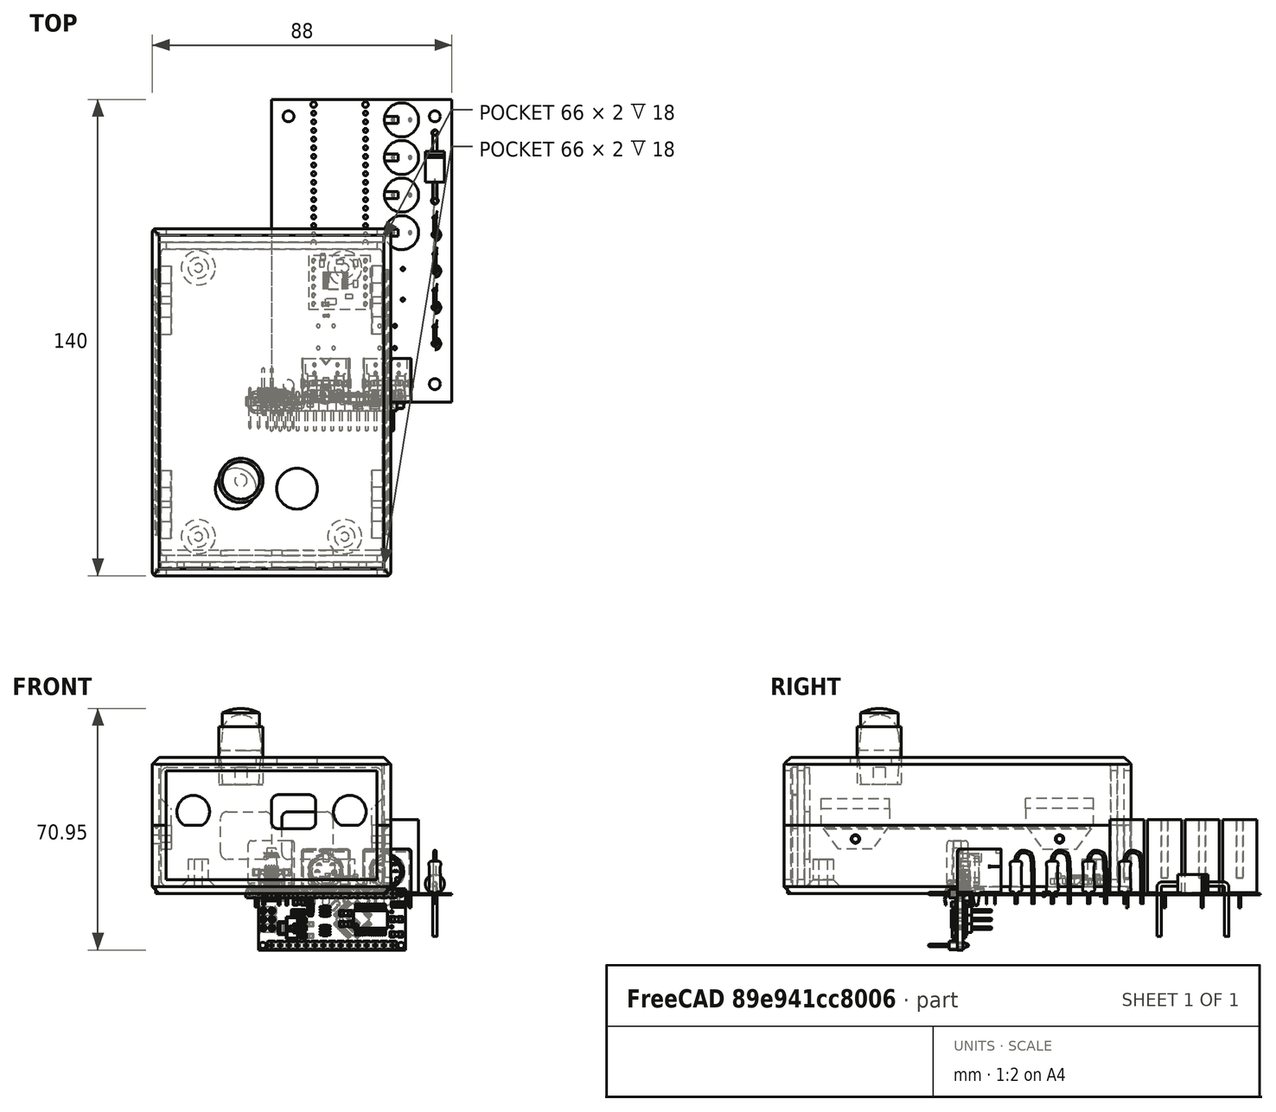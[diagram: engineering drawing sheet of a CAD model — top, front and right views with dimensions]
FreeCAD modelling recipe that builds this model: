
FCSTD DOCUMENT  (FreeCAD 1.0R39109 (Git))
Label: box
License: All rights reserved
LicenseURL: https://en.wikipedia.org/wiki/All_rights_reserved
objects: Part::Feature×156, App::Part×50, Sketcher::SketchObject×21, PartDesign::Pocket×11, PartDesign::Pad×7, PartDesign::Mirrored×7, App::Link×7, App::FeaturePython×7, PartDesign::Fillet×6, PartDesign::Body×6, PartDesign::Chamfer×5, PartDesign::Plane×2, PartDesign::Revolution×2, Mesh::Feature×1, PartDesign::MultiTransform×1, Assembly::JointGroup×1, Assembly::AssemblyObject×1
note: 315 computed .brp shape members not serialized (recipe doc carries the construction recipe); baked Part::Feature solids carry a one-line shape summary decoded from their .brp

FEATURE [Part::Feature] Part__Feature  label="Open CASCADE STEP translator 7.5 1.1.1"
  Placement = pos=(0,0,-0.41148) rot=(0,0,1;0rad)
  shape: bbox 53 x 89 x 0.4115 mm, 116 faces (baked)
FEATURE [App::Part] Board
  Group = -> [Part__Feature]
  Origin = -> Origin
FEATURE [Part::Feature] Part__Feature001  label="R603"
  Placement = pos=(34.1248,25.4,0) rot=(0,0.707107,0.707107;3.14159rad)
  shape: bbox 1.6 x 0.8 x 0.302 mm, 90 faces (baked)
FEATURE [App::Part] R4
  Group = -> [Part__Feature001]
  Origin = -> Origin001
FEATURE [Part::Feature] Part__Feature002  label="C0603"
  Placement = pos=(33.2994,25.7937,-0.41148) rot=(-1,0,0;1.5708rad)
  shape: bbox 1.6 x 0.8 x 0.5 mm, 44 faces (baked)
FEATURE [App::Part] C2
  Group = -> [Part__Feature002]
  Origin = -> Origin002
FEATURE [Part::Feature] Part__Feature003  label="R604"
  Placement = pos=(16.0749,25.3999,0) rot=(0,0.707107,0.707107;3.14159rad)
  shape: bbox 1.6 x 0.8 x 0.302 mm, 90 faces (baked)
FEATURE [App::Part] R3
  Group = -> [Part__Feature003]
  Origin = -> Origin003
FEATURE [Part::Feature] Part__Feature004  label="C0604"
  Placement = pos=(15.2994,25.7937,-0.41148) rot=(-1,0,0;1.5708rad)
  shape: bbox 1.6 x 0.8 x 0.5 mm, 44 faces (baked)
FEATURE [App::Part] C1
  Group = -> [Part__Feature004]
  Origin = -> Origin004
FEATURE [Part::Feature] Part__Feature005  label="1"
  shape: bbox 0.6 x 0.6 x 4.5 mm, 4 faces (baked)
FEATURE [Part::Feature] Part__Feature006  label="1001"
  shape: bbox 0.6 x 0.6 x 4 mm, 4 faces (baked)
FEATURE [App::Part] _  label="1002"
  Group = -> [Part__Feature005,Part__Feature006]
  Origin = -> Origin005
FEATURE [Part::Feature] Part__Feature007  label="2"
  shape: bbox 11.96 x 4.66 x 0.5 mm, 10 faces (baked)
FEATURE [Part::Feature] Part__Feature008  label="3"
  shape: bbox 0.8199 x 2.3 x 15.48 mm, 17 faces (baked)
FEATURE [Part::Feature] Part__Feature009  label="4"
  shape: bbox 13.93 x 6.63 x 15.5 mm, 101 faces (baked)
FEATURE [Part::Feature] Part__Feature010  label="AVX Logo 2"
  Placement = pos=(2.33024,3.051,15.4348) rot=(0,0.707107,0.707107;3.14159rad)
  shape: bbox 0.9574 x 0.1 x 1.177 mm, 8 faces (baked)
FEATURE [Part::Feature] Part__Feature011  label="AVX Logo 003"
  Placement = pos=(2.33024,3.051,15.4348) rot=(0,0.707107,0.707107;3.14159rad)
  shape: bbox 0.6063 x 0.1 x 1.597 mm, 8 faces (baked)
FEATURE [Part::Feature] Part__Feature012  label="AVX Logo 004"
  Placement = pos=(2.33024,3.051,15.4348) rot=(0,0.707107,0.707107;3.14159rad)
  shape: bbox 0.9677 x 0.1 x 0.5254 mm, 10 faces (baked)
FEATURE [Part::Feature] Part__Feature013  label="AVX Logo 005"
  Placement = pos=(2.33024,3.051,15.4348) rot=(0,0.707107,0.707107;3.14159rad)
  shape: bbox 0.3209 x 0.1 x 0.3907 mm, 5 faces (baked)
FEATURE [Part::Feature] Part__Feature014  label="AVX Logo 006"
  Placement = pos=(2.33024,3.051,15.4348) rot=(0,0.707107,0.707107;3.14159rad)
  shape: bbox 0.2898 x 0.1 x 0.3547 mm, 5 faces (baked)
FEATURE [Part::Feature] Part__Feature015  label="AVX Logo 007"
  Placement = pos=(2.33024,3.051,15.4348) rot=(0,0.707107,0.707107;3.14159rad)
  shape: bbox 0.3208 x 0.1 x 0.3911 mm, 5 faces (baked)
FEATURE [Part::Feature] Part__Feature016  label="AVX Logo 008"
  Placement = pos=(2.33024,3.051,15.4348) rot=(0,0.707107,0.707107;3.14159rad)
  shape: bbox 0.9255 x 0.1 x 1.591 mm, 6 faces (baked)
FEATURE [Part::Feature] Part__Feature017  label="AVX Logo 009"
  Placement = pos=(2.33024,3.051,15.4348) rot=(0,0.707107,0.707107;3.14159rad)
  shape: bbox 0.9743 x 0.1 x 1.58 mm, 6 faces (baked)
FEATURE [Part::Feature] Part__Feature018  label="AVX Logo 010"
  Placement = pos=(2.33024,3.051,15.4348) rot=(0,0.707107,0.707107;3.14159rad)
  shape: bbox 1.209 x 0.1 x 1.602 mm, 11 faces (baked)
FEATURE [App::Part] AVX_Logo_2  label="AVX Logo 011"
  Group = -> [Part__Feature010,Part__Feature011,Part__Feature012,Part__Feature013,Part__Feature014,Part__Feature015,Part__Feature016,Part__Feature017,Part__Feature018]
  Origin = -> Origin006
FEATURE [App::Part] Cap_AVX_SCMQ14C474PRBA0_eec
  Group = -> [_,Part__Feature007,Part__Feature008,Part__Feature009,AVX_Logo_2]
  Origin = -> Origin007
  Placement = pos=(38.608,34.6712,0) rot=(0,0,-1;1.5708rad)
FEATURE [App::Part] C7
  Group = -> [Cap_AVX_SCMQ14C474PRBA0_eec]
  Origin = -> Origin008
FEATURE [Part::Feature] Part__Feature019  label="DO-201AD"
  Placement = pos=(48,69.1712,0) rot=(0.57735,-0.57735,-0.57735;2.0944rad)
  shape: bbox 5.6 x 0.8 x 5.6 mm, 6 faces (baked)
FEATURE [Part::Feature] Part__Feature020  label="DO-201AD001"
  Placement = pos=(48,69.1712,0) rot=(0.57735,-0.57735,-0.57735;2.0944rad)
  shape: bbox 5.6 x 9 x 5.6 mm, 10 faces (baked)
FEATURE [Part::Feature] Part__Feature021  label="DO-201AD002"
  Placement = pos=(48,69.1712,0) rot=(0.57735,-0.57735,-0.57735;2.0944rad)
  shape: bbox 1.25 x 6.209 x 16.21 mm, 8 faces (baked)
FEATURE [Part::Feature] Part__Feature022  label="DO-201AD003"
  Placement = pos=(48,69.1712,0) rot=(0.57735,-0.57735,-0.57735;2.0944rad)
  shape: bbox 1.25 x 6.209 x 16.21 mm, 8 faces (baked)
FEATURE [App::Part] DO_201AD  label="DO-201AD004"
  Group = -> [Part__Feature019,Part__Feature020,Part__Feature021,Part__Feature022]
  Origin = -> Origin009
FEATURE [App::Part] D3
  Group = -> [DO_201AD]
  Origin = -> Origin010
FEATURE [Part::Feature] Part__Feature023  label="RESISTOR_2W_VERTICALE"
  Placement = pos=(48.0001,27.8623,22) rot=(0.57735,-0.57735,-0.57735;2.0944rad)
  shape: bbox 7.092 x 7.627 x 16.21 mm, 28 faces (baked)
FEATURE [App::Part] R8
  Group = -> [Part__Feature023]
  Origin = -> Origin011
FEATURE [Part::Feature] Part__Feature024  label="RESISTOR_2W_VERTICALE001"
  Placement = pos=(48.0001,17.1892,22) rot=(0.57735,-0.57735,-0.57735;2.0944rad)
  shape: bbox 7.092 x 7.627 x 16.21 mm, 28 faces (baked)
FEATURE [App::Part] R7
  Group = -> [Part__Feature024]
  Origin = -> Origin012
FEATURE [Part::Feature] Part__Feature025  label="RESISTOR_2W_VERTICALE002"
  Placement = pos=(48.0001,49.2084,22) rot=(0.57735,-0.57735,-0.57735;2.0944rad)
  shape: bbox 7.092 x 7.627 x 16.21 mm, 28 faces (baked)
FEATURE [App::Part] R6
  Group = -> [Part__Feature025]
  Origin = -> Origin013
FEATURE [Part::Feature] Part__Feature026  label="RESISTOR_2W_VERTICALE003"
  Placement = pos=(48.0001,38.5353,22) rot=(0.57735,-0.57735,-0.57735;2.0944rad)
  shape: bbox 7.092 x 7.627 x 16.21 mm, 28 faces (baked)
FEATURE [App::Part] R5
  Group = -> [Part__Feature026]
  Origin = -> Origin014
FEATURE [Part::Feature] Part__Feature027  label="CAP_RN_10X20_NCH"
  Placement = pos=(40.727,60.873,0.2) rot=(0,0,1;3.14159rad)
  shape: bbox 0.6096 x 0.6096 x 4.369 mm, 3 faces (baked)
FEATURE [Part::Feature] Part__Feature028  label="CAP_RN_10X20_NCH001"
  Placement = pos=(40.727,60.873,0.2) rot=(0,0,1;3.14159rad)
  shape: bbox 0.6096 x 0.6096 x 4.369 mm, 3 faces (baked)
FEATURE [Part::Feature] Part__Feature029  label="CAP_RN_10X20_NCH002"
  Placement = pos=(40.727,60.873,0.2) rot=(0,0,1;3.14159rad)
  shape: bbox 10.01 x 10.01 x 21.49 mm, 3 faces (baked)
FEATURE [Part::Feature] Part__Feature030  label="CAP_RN_10X20_NCH003"
  Placement = pos=(40.727,60.873,0.2) rot=(0,0,1;3.14159rad)
  shape: bbox 4.029 x 1.953 x 17.22 mm, 8 faces (baked)
FEATURE [App::Part] CAP_RN_10X20_NCH  label="CAP_RN_10X20_NCH004"
  Group = -> [Part__Feature027,Part__Feature028,Part__Feature029,Part__Feature030]
  Origin = -> Origin015
FEATURE [App::Part] C5
  Group = -> [CAP_RN_10X20_NCH]
  Origin = -> Origin016
FEATURE [Part::Feature] Part__Feature031  label="CAP_RN_10X20_NCH005"
  Placement = pos=(40.727,71.922,0.2) rot=(0,0,1;3.14159rad)
  shape: bbox 0.6096 x 0.6096 x 4.369 mm, 3 faces (baked)
FEATURE [Part::Feature] Part__Feature032  label="CAP_RN_10X20_NCH006"
  Placement = pos=(40.727,71.922,0.2) rot=(0,0,1;3.14159rad)
  shape: bbox 0.6096 x 0.6096 x 4.369 mm, 3 faces (baked)
FEATURE [Part::Feature] Part__Feature033  label="CAP_RN_10X20_NCH007"
  Placement = pos=(40.727,71.922,0.2) rot=(0,0,1;3.14159rad)
  shape: bbox 10.01 x 10.01 x 21.49 mm, 3 faces (baked)
FEATURE [Part::Feature] Part__Feature034  label="CAP_RN_10X20_NCH008"
  Placement = pos=(40.727,71.922,0.2) rot=(0,0,1;3.14159rad)
  shape: bbox 4.029 x 1.953 x 17.22 mm, 8 faces (baked)
FEATURE [App::Part] CAP_RN_10X20_NCH001  label="CAP_RN_10X20_NCH009"
  Group = -> [Part__Feature031,Part__Feature032,Part__Feature033,Part__Feature034]
  Origin = -> Origin017
FEATURE [App::Part] C4
  Group = -> [CAP_RN_10X20_NCH001]
  Origin = -> Origin018
FEATURE [Part::Feature] Part__Feature035  label="CAP_RN_10X20_NCH010"
  Placement = pos=(40.727,82.971,0.2) rot=(0,0,1;3.14159rad)
  shape: bbox 0.6096 x 0.6096 x 4.369 mm, 3 faces (baked)
FEATURE [Part::Feature] Part__Feature036  label="CAP_RN_10X20_NCH011"
  Placement = pos=(40.727,82.971,0.2) rot=(0,0,1;3.14159rad)
  shape: bbox 0.6096 x 0.6096 x 4.369 mm, 3 faces (baked)
FEATURE [Part::Feature] Part__Feature037  label="CAP_RN_10X20_NCH012"
  Placement = pos=(40.727,82.971,0.2) rot=(0,0,1;3.14159rad)
  shape: bbox 10.01 x 10.01 x 21.49 mm, 3 faces (baked)
FEATURE [Part::Feature] Part__Feature038  label="CAP_RN_10X20_NCH013"
  Placement = pos=(40.727,82.971,0.2) rot=(0,0,1;3.14159rad)
  shape: bbox 4.029 x 1.953 x 17.22 mm, 8 faces (baked)
FEATURE [App::Part] CAP_RN_10X20_NCH002  label="CAP_RN_10X20_NCH014"
  Group = -> [Part__Feature035,Part__Feature036,Part__Feature037,Part__Feature038]
  Origin = -> Origin019
FEATURE [App::Part] C3
  Group = -> [CAP_RN_10X20_NCH002]
  Origin = -> Origin020
FEATURE [Part::Feature] Part__Feature039  label="CAP_RN_10X20_NCH015"
  Placement = pos=(40.727,49.824,0.2) rot=(0,0,1;3.14159rad)
  shape: bbox 0.6096 x 0.6096 x 4.369 mm, 3 faces (baked)
FEATURE [Part::Feature] Part__Feature040  label="CAP_RN_10X20_NCH016"
  Placement = pos=(40.727,49.824,0.2) rot=(0,0,1;3.14159rad)
  shape: bbox 0.6096 x 0.6096 x 4.369 mm, 3 faces (baked)
FEATURE [Part::Feature] Part__Feature041  label="CAP_RN_10X20_NCH017"
  Placement = pos=(40.727,49.824,0.2) rot=(0,0,1;3.14159rad)
  shape: bbox 10.01 x 10.01 x 21.49 mm, 3 faces (baked)
FEATURE [Part::Feature] Part__Feature042  label="CAP_RN_10X20_NCH018"
  Placement = pos=(40.727,49.824,0.2) rot=(0,0,1;3.14159rad)
  shape: bbox 4.029 x 1.953 x 17.22 mm, 8 faces (baked)
FEATURE [App::Part] CAP_RN_10X20_NCH003  label="CAP_RN_10X20_NCH019"
  Group = -> [Part__Feature039,Part__Feature040,Part__Feature041,Part__Feature042]
  Origin = -> Origin021
FEATURE [App::Part] C6
  Group = -> [CAP_RN_10X20_NCH003]
  Origin = -> Origin022
FEATURE [Part::Feature] Part__Feature043  label="arm"
  Placement = pos=(0,0,13) rot=(0,0,1;0rad)
  shape: bbox 3.51 x 3.51 x 9.7 mm, 4 faces (baked)
FEATURE [Part::Feature] Part__Feature044  label="body"
  Placement = pos=(0,0,13) rot=(0,0,1;0rad)
  shape: bbox 5.99 x 5.99 x 3.9 mm, 22 faces (baked)
FEATURE [Part::Feature] Part__Feature045  label="leads"
  Placement = pos=(0,0,13) rot=(0,0,1;0rad)
  shape: bbox 0.71 x 0.905 x 4.81 mm, 16 faces (baked)
FEATURE [Part::Feature] Part__Feature046  label="leads001"
  Placement = pos=(0,0,13) rot=(0,0,1;0rad)
  shape: bbox 0.71 x 0.905 x 4.81 mm, 16 faces (baked)
FEATURE [Part::Feature] Part__Feature047  label="leads002"
  Placement = pos=(0,0,13) rot=(0,0,1;0rad)
  shape: bbox 0.71 x 0.905 x 4.81 mm, 16 faces (baked)
FEATURE [Part::Feature] Part__Feature048  label="leads003"
  Placement = pos=(0,0,13) rot=(0,0,1;0rad)
  shape: bbox 0.71 x 0.905 x 4.81 mm, 16 faces (baked)
FEATURE [App::Part] leads  label="leads004"
  Group = -> [Part__Feature045,Part__Feature046,Part__Feature047,Part__Feature048]
  Origin = -> Origin023
FEATURE [Part::Feature] Part__Feature049  label="top"
  Placement = pos=(0,0,13) rot=(0,0,1;0rad)
  shape: bbox 5.99 x 5.99 x 0.1 mm, 14 faces (baked)
FEATURE [Part::Feature] Part__Feature050  label="TE Connectivity"
  Placement = pos=(-2.995,0.1796,1.65363) rot=(0.57735,-0.57735,-0.57735;2.0944rad)
  shape: bbox 0.003004 x 0.8535 x 0.7964 mm, 15 faces (baked)
FEATURE [Part::Feature] Part__Feature051  label="TE Connectivity001"
  Placement = pos=(-2.995,0.1796,1.65363) rot=(0.57735,-0.57735,-0.57735;2.0944rad)
  shape: bbox 0.003 x 0.7442 x 0.7964 mm, 11 faces (baked)
FEATURE [Part::Feature] Part__Feature052  label="TE Connectivity002"
  Placement = pos=(-2.995,0.1796,1.65363) rot=(0.57735,-0.57735,-0.57735;2.0944rad)
  shape: bbox 0.003601 x 1.019 x 0.2312 mm, 10 faces (baked)
FEATURE [Part::Feature] Part__Feature053  label="TE Connectivity003"
  Placement = pos=(-2.995,0.1796,1.65363) rot=(0.57735,-0.57735,-0.57735;2.0944rad)
  shape: bbox 0.0036 x 1.019 x 0.2312 mm, 8 faces (baked)
FEATURE [Part::Feature] Part__Feature054  label="TE Connectivity004"
  Placement = pos=(-2.995,0.1796,1.65363) rot=(0.57735,-0.57735,-0.57735;2.0944rad)
  shape: bbox 0.0036 x 1.019 x 0.2312 mm, 8 faces (baked)
FEATURE [Part::Feature] Part__Feature055  label="TE Connectivity005"
  Placement = pos=(-2.995,0.1796,1.65363) rot=(0.57735,-0.57735,-0.57735;2.0944rad)
  shape: bbox 0.003645 x 0.1539 x 0.16 mm, 13 faces (baked)
FEATURE [Part::Feature] Part__Feature056  label="TE Connectivity006"
  Placement = pos=(-2.995,0.1796,1.65363) rot=(0.57735,-0.57735,-0.57735;2.0944rad)
  shape: bbox 0.00365 x 0.1344 x 0.1238 mm, 18 faces (baked)
FEATURE [Part::Feature] Part__Feature057  label="TE Connectivity007"
  Placement = pos=(-2.995,0.1796,1.65363) rot=(0.57735,-0.57735,-0.57735;2.0944rad)
  shape: bbox 0.003601 x 0.1303 x 0.1287 mm, 16 faces (baked)
FEATURE [Part::Feature] Part__Feature058  label="TE Connectivity008"
  Placement = pos=(-2.995,0.1796,1.65363) rot=(0.57735,-0.57735,-0.57735;2.0944rad)
  shape: bbox 0.003684 x 0.1335 x 0.1245 mm, 18 faces (baked)
FEATURE [Part::Feature] Part__Feature059  label="TE Connectivity009"
  Placement = pos=(-2.995,0.1796,1.65363) rot=(0.57735,-0.57735,-0.57735;2.0944rad)
  shape: bbox 0.003695 x 0.1252 x 0.1305 mm, 16 faces (baked)
FEATURE [Part::Feature] Part__Feature060  label="TE Connectivity010"
  Placement = pos=(-2.995,0.1796,1.65363) rot=(0.57735,-0.57735,-0.57735;2.0944rad)
  shape: bbox 0.004453 x 0.08777 x 0.1574 mm, 23 faces (baked)
FEATURE [Part::Feature] Part__Feature061  label="TE Connectivity011"
  Placement = pos=(-2.995,0.1796,1.65363) rot=(0.57735,-0.57735,-0.57735;2.0944rad)
  shape: bbox 0.003603 x 0.1223 x 0.1299 mm, 15 faces (baked)
FEATURE [Part::Feature] Part__Feature062  label="TE Connectivity012"
  Placement = pos=(-2.995,0.1796,1.65363) rot=(0.57735,-0.57735,-0.57735;2.0944rad)
  shape: bbox 0.003805 x 0.1229 x 0.1291 mm, 20 faces (baked)
FEATURE [Part::Feature] Part__Feature063  label="TE Connectivity013"
  Placement = pos=(-2.995,0.1796,1.65363) rot=(0.57735,-0.57735,-0.57735;2.0944rad)
  shape: bbox 0.003627 x 0.0856 x 0.1551 mm, 24 faces (baked)
FEATURE [Part::Feature] Part__Feature064  label="TE Connectivity014"
  Placement = pos=(-2.995,0.1796,1.65363) rot=(0.57735,-0.57735,-0.57735;2.0944rad)
  shape: bbox 0.003 x 0.1246 x 0.1226 mm, 9 faces (baked)
FEATURE [Part::Feature] Part__Feature065  label="TE Connectivity015"
  Placement = pos=(-2.995,0.1796,1.65363) rot=(0.57735,-0.57735,-0.57735;2.0944rad)
  shape: bbox 0.003 x 0.0679 x 0.1237 mm, 6 faces (baked)
FEATURE [Part::Feature] Part__Feature066  label="TE Connectivity016"
  Placement = pos=(-2.995,0.1796,1.65363) rot=(0.57735,-0.57735,-0.57735;2.0944rad)
  shape: bbox 0.003 x 0.06666 x 0.1243 mm, 6 faces (baked)
FEATURE [Part::Feature] Part__Feature067  label="TE Connectivity017"
  Placement = pos=(-2.995,0.1796,1.65363) rot=(0.57735,-0.57735,-0.57735;2.0944rad)
  shape: bbox 0.003 x 0.04472 x 0.03068 mm, 6 faces (baked)
FEATURE [App::Part] TE_Connectivity  label="TE Connectivity018"
  Group = -> [Part__Feature050,Part__Feature051,Part__Feature052,Part__Feature053,Part__Feature054,Part__Feature055,Part__Feature056,Part__Feature057,Part__Feature058,Part__Feature059,Part__Feature060,Part__Feature061,Part__Feature062,Part__Feature063,Part__Feature064,Part__Feature065,Part__Feature066,Part__Feature067]
  Origin = -> Origin024
FEATURE [App::Part] Switch_TE_Connectivity_2_1825910_7_eec  label="Switch_TE_Connectivity_2-1825910-7_eec"
  Group = -> [Part__Feature043,Part__Feature044,leads,Part__Feature049,TE_Connectivity]
  Origin = -> Origin025
  Placement = pos=(34,19.177,0) rot=(0,0,1;0rad)
FEATURE [App::Part] SW2
  Group = -> [Switch_TE_Connectivity_2_1825910_7_eec]
  Origin = -> Origin026
FEATURE [Part::Feature] Part__Feature068  label="arm001"
  Placement = pos=(0,0,13) rot=(0,0,1;0rad)
  shape: bbox 3.51 x 3.51 x 9.7 mm, 4 faces (baked)
FEATURE [Part::Feature] Part__Feature069  label="body001"
  Placement = pos=(0,0,13) rot=(0,0,1;0rad)
  shape: bbox 5.99 x 5.99 x 3.9 mm, 22 faces (baked)
FEATURE [Part::Feature] Part__Feature070  label="leads005"
  Placement = pos=(0,0,13) rot=(0,0,1;0rad)
  shape: bbox 0.71 x 0.905 x 4.81 mm, 16 faces (baked)
FEATURE [Part::Feature] Part__Feature071  label="leads006"
  Placement = pos=(0,0,13) rot=(0,0,1;0rad)
  shape: bbox 0.71 x 0.905 x 4.81 mm, 16 faces (baked)
FEATURE [Part::Feature] Part__Feature072  label="leads007"
  Placement = pos=(0,0,13) rot=(0,0,1;0rad)
  shape: bbox 0.71 x 0.905 x 4.81 mm, 16 faces (baked)
FEATURE [Part::Feature] Part__Feature073  label="leads008"
  Placement = pos=(0,0,13) rot=(0,0,1;0rad)
  shape: bbox 0.71 x 0.905 x 4.81 mm, 16 faces (baked)
FEATURE [App::Part] leads001  label="leads009"
  Group = -> [Part__Feature070,Part__Feature071,Part__Feature072,Part__Feature073]
  Origin = -> Origin027
FEATURE [Part::Feature] Part__Feature074  label="top001"
  Placement = pos=(0,0,13) rot=(0,0,1;0rad)
  shape: bbox 5.99 x 5.99 x 0.1 mm, 14 faces (baked)
FEATURE [Part::Feature] Part__Feature075  label="TE Connectivity019"
  Placement = pos=(-2.995,0.1796,1.65363) rot=(0.57735,-0.57735,-0.57735;2.0944rad)
  shape: bbox 0.003004 x 0.8535 x 0.7964 mm, 15 faces (baked)
FEATURE [Part::Feature] Part__Feature076  label="TE Connectivity020"
  Placement = pos=(-2.995,0.1796,1.65363) rot=(0.57735,-0.57735,-0.57735;2.0944rad)
  shape: bbox 0.003 x 0.7442 x 0.7964 mm, 11 faces (baked)
FEATURE [Part::Feature] Part__Feature077  label="TE Connectivity021"
  Placement = pos=(-2.995,0.1796,1.65363) rot=(0.57735,-0.57735,-0.57735;2.0944rad)
  shape: bbox 0.003601 x 1.019 x 0.2312 mm, 10 faces (baked)
FEATURE [Part::Feature] Part__Feature078  label="TE Connectivity022"
  Placement = pos=(-2.995,0.1796,1.65363) rot=(0.57735,-0.57735,-0.57735;2.0944rad)
  shape: bbox 0.0036 x 1.019 x 0.2312 mm, 8 faces (baked)
FEATURE [Part::Feature] Part__Feature079  label="TE Connectivity023"
  Placement = pos=(-2.995,0.1796,1.65363) rot=(0.57735,-0.57735,-0.57735;2.0944rad)
  shape: bbox 0.0036 x 1.019 x 0.2312 mm, 8 faces (baked)
FEATURE [Part::Feature] Part__Feature080  label="TE Connectivity024"
  Placement = pos=(-2.995,0.1796,1.65363) rot=(0.57735,-0.57735,-0.57735;2.0944rad)
  shape: bbox 0.003645 x 0.1539 x 0.16 mm, 13 faces (baked)
FEATURE [Part::Feature] Part__Feature081  label="TE Connectivity025"
  Placement = pos=(-2.995,0.1796,1.65363) rot=(0.57735,-0.57735,-0.57735;2.0944rad)
  shape: bbox 0.00365 x 0.1344 x 0.1238 mm, 18 faces (baked)
FEATURE [Part::Feature] Part__Feature082  label="TE Connectivity026"
  Placement = pos=(-2.995,0.1796,1.65363) rot=(0.57735,-0.57735,-0.57735;2.0944rad)
  shape: bbox 0.003601 x 0.1303 x 0.1287 mm, 16 faces (baked)
FEATURE [Part::Feature] Part__Feature083  label="TE Connectivity027"
  Placement = pos=(-2.995,0.1796,1.65363) rot=(0.57735,-0.57735,-0.57735;2.0944rad)
  shape: bbox 0.003684 x 0.1335 x 0.1245 mm, 18 faces (baked)
FEATURE [Part::Feature] Part__Feature084  label="TE Connectivity028"
  Placement = pos=(-2.995,0.1796,1.65363) rot=(0.57735,-0.57735,-0.57735;2.0944rad)
  shape: bbox 0.003695 x 0.1252 x 0.1305 mm, 16 faces (baked)
FEATURE [Part::Feature] Part__Feature085  label="TE Connectivity029"
  Placement = pos=(-2.995,0.1796,1.65363) rot=(0.57735,-0.57735,-0.57735;2.0944rad)
  shape: bbox 0.004453 x 0.08777 x 0.1574 mm, 23 faces (baked)
FEATURE [Part::Feature] Part__Feature086  label="TE Connectivity030"
  Placement = pos=(-2.995,0.1796,1.65363) rot=(0.57735,-0.57735,-0.57735;2.0944rad)
  shape: bbox 0.003603 x 0.1223 x 0.1299 mm, 15 faces (baked)
FEATURE [Part::Feature] Part__Feature087  label="TE Connectivity031"
  Placement = pos=(-2.995,0.1796,1.65363) rot=(0.57735,-0.57735,-0.57735;2.0944rad)
  shape: bbox 0.003805 x 0.1229 x 0.1291 mm, 20 faces (baked)
FEATURE [Part::Feature] Part__Feature088  label="TE Connectivity032"
  Placement = pos=(-2.995,0.1796,1.65363) rot=(0.57735,-0.57735,-0.57735;2.0944rad)
  shape: bbox 0.003627 x 0.0856 x 0.1551 mm, 24 faces (baked)
FEATURE [Part::Feature] Part__Feature089  label="TE Connectivity033"
  Placement = pos=(-2.995,0.1796,1.65363) rot=(0.57735,-0.57735,-0.57735;2.0944rad)
  shape: bbox 0.003 x 0.1246 x 0.1226 mm, 9 faces (baked)
FEATURE [Part::Feature] Part__Feature090  label="TE Connectivity034"
  Placement = pos=(-2.995,0.1796,1.65363) rot=(0.57735,-0.57735,-0.57735;2.0944rad)
  shape: bbox 0.003 x 0.0679 x 0.1237 mm, 6 faces (baked)
FEATURE [Part::Feature] Part__Feature091  label="TE Connectivity035"
  Placement = pos=(-2.995,0.1796,1.65363) rot=(0.57735,-0.57735,-0.57735;2.0944rad)
  shape: bbox 0.003 x 0.06666 x 0.1243 mm, 6 faces (baked)
FEATURE [Part::Feature] Part__Feature092  label="TE Connectivity036"
  Placement = pos=(-2.995,0.1796,1.65363) rot=(0.57735,-0.57735,-0.57735;2.0944rad)
  shape: bbox 0.003 x 0.04472 x 0.03068 mm, 6 faces (baked)
FEATURE [App::Part] TE_Connectivity001  label="TE Connectivity037"
  Group = -> [Part__Feature075,Part__Feature076,Part__Feature077,Part__Feature078,Part__Feature079,Part__Feature080,Part__Feature081,Part__Feature082,Part__Feature083,Part__Feature084,Part__Feature085,Part__Feature086,Part__Feature087,Part__Feature088,Part__Feature089,Part__Feature090,Part__Feature091,Part__Feature092]
  Origin = -> Origin028
FEATURE [App::Part] Switch_TE_Connectivity_2_1825910_7_eec001  label="Switch_TE_Connectivity_2-1825910-7_eec001"
  Group = -> [Part__Feature068,Part__Feature069,leads001,Part__Feature074,TE_Connectivity001]
  Origin = -> Origin029
  Placement = pos=(16,19.177,0) rot=(0,0,1;0rad)
FEATURE [App::Part] SW1
  Group = -> [Switch_TE_Connectivity_2_1825910_7_eec001]
  Origin = -> Origin030
FEATURE [Part::Feature] Part__Feature093  label="R0805"
  Placement = pos=(15.113,42.567,-0.41148) rot=(-0.57735,0.57735,-0.57735;2.0944rad)
  shape: bbox 1.26 x 2 x 0.46 mm, 16 faces (baked)
FEATURE [App::Part] R1
  Group = -> [Part__Feature093]
  Origin = -> Origin031
FEATURE [Part::Feature] Part__Feature094  label="R0806"
  Placement = pos=(15.859,28.829,-0.41148) rot=(0,0.707107,-0.707107;3.14159rad)
  shape: bbox 2 x 1.26 x 0.46 mm, 16 faces (baked)
FEATURE [App::Part] R2
  Group = -> [Part__Feature094]
  Origin = -> Origin032
FEATURE [Part::Feature] Part__Feature095  label="Open CASCADE STEP translator 7.5 1.20.1.1"
  shape: bbox 15.24 x 12.12 x 2.5 mm, 278 faces (baked)
FEATURE [App::Part] Molex_90120_0126  label="Molex 90120-0126"
  Group = -> [Part__Feature095]
  Origin = -> Origin033
  Placement = pos=(27.6201,35.2172,1.2) rot=(0.57735,0.57735,0.57735;2.0944rad)
FEATURE [Part::Feature] Part__Feature096  label="Open CASCADE STEP translator 7.5 1.20.1.002"
  shape: bbox 15.24 x 12.12 x 2.5 mm, 278 faces (baked)
FEATURE [App::Part] Molex_90120_0127  label="Molex 90120-0127"
  Group = -> [Part__Feature096]
  Origin = -> Origin034
  Placement = pos=(12.3801,35.2172,1.2) rot=(0.57735,0.57735,0.57735;2.0944rad)
FEATURE [Part::Feature] Part__Feature097  label="DRV8833 Motor Driver Module"
  Placement = pos=(20,35.2172,4.4) rot=(0,0,1;0rad)
  shape: bbox 18.2 x 15.7 x 3.1 mm, 60 faces (baked)
FEATURE [Part::Feature] Part__Feature098  label="DRV8833 Motor Driver Module001"
  Placement = pos=(20,35.2172,4.4) rot=(0,0,1;0rad)
  shape: bbox 7.131 x 5 x 1.037 mm, 109 faces (baked)
FEATURE [App::Part] DRV8833_Motor_Driver_Module  label="DRV8833 Motor Driver Module002"
  Group = -> [Part__Feature097,Part__Feature098]
  Origin = -> Origin035
FEATURE [App::Part] U2
  Group = -> [Molex_90120_0126,Molex_90120_0127,DRV8833_Motor_Driver_Module]
  Origin = -> Origin036
FEATURE [Part::Feature] Part__Feature099  label="nano-board"
  shape: bbox 43.2 x 4.77 x 18 mm, 378 faces (baked)
FEATURE [Part::Feature] Part__Feature100  label="2pin_header__02"
  Placement = pos=(-1.143,1.6,-7.62) rot=(0,0,1;0rad)
  shape: bbox 5 x 11.75 x 2.54 mm, 46 faces (baked)
FEATURE [Part::Feature] Part__Feature101  label="2pin_header__003"
  Placement = pos=(-1.143,1.6,-5.08) rot=(0,0,1;0rad)
  shape: bbox 5 x 11.75 x 2.54 mm, 46 faces (baked)
FEATURE [Part::Feature] Part__Feature102  label="2pin_header__004"
  Placement = pos=(-1.143,1.6,-10.16) rot=(0,0,1;0rad)
  shape: bbox 5 x 11.75 x 2.54 mm, 46 faces (baked)
FEATURE [Part::Feature] Part__Feature103  label="15pin_header__"
  Placement = pos=(0,0,0) rot=(0.707107,0,0.707107;3.14159rad)
  shape: bbox 38.1 x 11.75 x 2.54 mm, 364 faces (baked)
FEATURE [Part::Feature] Part__Feature104  label="15pin_header__001"
  Placement = pos=(-2.5e-15,0,-15.24) rot=(0.707107,0,0.707107;3.14159rad)
  shape: bbox 38.1 x 11.75 x 2.54 mm, 364 faces (baked)
FEATURE [Part::Feature] Part__Feature105  label="atmega328"
  Placement = pos=(23.85,1.75,-7.62) rot=(0,1,0;3.92699rad)
  shape: bbox 11.25 x 1.2 x 11.25 mm, 1867 faces (baked)
FEATURE [Part::Feature] Part__Feature106  label="ftdi FT232rl"
  Placement = pos=(29.05,1e-16,-7.67) rot=(0.707107,0,-0.707107;3.14159rad)
  shape: bbox 10.2 x 1.9 x 9.287 mm, 717 faces (baked)
FEATURE [Part::Feature] Part__Feature107  label="smt_resistor222"
  Placement = pos=(21.86,0,-5.8) rot=(0.707107,0,-0.707107;3.14159rad)
  shape: bbox 3.8 x 0.6 x 1.813 mm, 74 faces (baked)
FEATURE [Part::Feature] Part__Feature108  label="smt_resistor223"
  Placement = pos=(21.86,0,-9) rot=(0.707107,0,-0.707107;3.14159rad)
  shape: bbox 3.8 x 0.6 x 1.813 mm, 74 faces (baked)
FEATURE [Part::Feature] Part__Feature109  label="smt_resistor224"
  Placement = pos=(36.75,0,-7.6) rot=(0.707107,0,-0.707107;3.14159rad)
  shape: bbox 3.8 x 0.6 x 1.813 mm, 74 faces (baked)
FEATURE [Part::Feature] Part__Feature110  label="smt_resistor225"
  Placement = pos=(36.75,0,-12) rot=(0.707107,0,-0.707107;3.14159rad)
  shape: bbox 3.8 x 0.6 x 1.813 mm, 74 faces (baked)
FEATURE [Part::Feature] Part__Feature111  label="smt_resistor226"
  Placement = pos=(8.2,0,-2.6) rot=(0.707107,0,-0.707107;3.14159rad)
  shape: bbox 3.8 x 0.6 x 1.813 mm, 74 faces (baked)
FEATURE [Part::Feature] Part__Feature112  label="led"
  Placement = pos=(10.4,1.6,-2.8) rot=(0,0,1;0rad)
  shape: bbox 4.438 x 0.5452 x 2.138 mm, 51 faces (baked)
FEATURE [Part::Feature] Part__Feature113  label="led001"
  Placement = pos=(10.4,1.6,-2.8) rot=(0,0,1;0rad)
  shape: bbox 1.4 x 0.5 x 1.2 mm, 6 faces (baked)
FEATURE [App::Part] led  label="led002"
  Group = -> [Part__Feature112,Part__Feature113]
  Origin = -> Origin037
FEATURE [Part::Feature] Part__Feature114  label="led003"
  Placement = pos=(10.4,1.6,-5.55) rot=(0,0,1;0rad)
  shape: bbox 4.438 x 0.5452 x 2.138 mm, 51 faces (baked)
FEATURE [Part::Feature] Part__Feature115  label="led004"
  Placement = pos=(10.4,1.6,-5.55) rot=(0,0,1;0rad)
  shape: bbox 1.4 x 0.5 x 1.2 mm, 6 faces (baked)
FEATURE [App::Part] led001  label="led005"
  Group = -> [Part__Feature114,Part__Feature115]
  Origin = -> Origin038
FEATURE [Part::Feature] Part__Feature116  label="led006"
  Placement = pos=(10.4,1.6,-12.5) rot=(0,0,1;0rad)
  shape: bbox 4.438 x 0.5452 x 2.138 mm, 51 faces (baked)
FEATURE [Part::Feature] Part__Feature117  label="led007"
  Placement = pos=(10.4,1.6,-12.5) rot=(0,0,1;0rad)
  shape: bbox 1.4 x 0.5 x 1.2 mm, 6 faces (baked)
FEATURE [App::Part] led002  label="led008"
  Group = -> [Part__Feature116,Part__Feature117]
  Origin = -> Origin039
FEATURE [Part::Feature] Part__Feature118  label="led009"
  Placement = pos=(10.4,1.6,-9.05) rot=(0,0,1;0rad)
  shape: bbox 4.438 x 0.5452 x 2.138 mm, 51 faces (baked)
FEATURE [Part::Feature] Part__Feature119  label="led010"
  Placement = pos=(10.4,1.6,-9.05) rot=(0,0,1;0rad)
  shape: bbox 1.4 x 0.5 x 1.2 mm, 6 faces (baked)
FEATURE [App::Part] led003  label="led011"
  Group = -> [Part__Feature118,Part__Feature119]
  Origin = -> Origin040
FEATURE [Part::Feature] Part__Feature120  label="16mhz crystal - measured"
  Placement = pos=(18.5113,1.6,-3.55414) rot=(0,-1,0;0.785398rad)
  shape: bbox 3.394 x 0.8 x 3.394 mm, 71 faces (baked)
FEATURE [Part::Feature] Part__Feature121  label="MINIUSBSHELL"
  shape: bbox 11.03 x 3.822 x 9.475 mm, 243 faces (baked)
FEATURE [Part::Feature] Part__Feature122  label="MINIUSBCORE"
  Placement = pos=(0,0,6.7) rot=(0,1,0;3.14159rad)
  shape: bbox 7.7 x 4.5 x 8.2 mm, 127 faces (baked)
FEATURE [Part::Feature] Part__Feature123  label="MINI USB CONTACT"
  Placement = pos=(-1.6,0,5.7) rot=(0,1,0;3.14159rad)
  shape: bbox 0.5011 x 2.551 x 9.423 mm, 31 faces (baked)
FEATURE [Part::Feature] Part__Feature124  label="MINI USB CONTACT001"
  Placement = pos=(-0.8,0,5.7) rot=(0,1,0;3.14159rad)
  shape: bbox 0.5011 x 2.551 x 9.423 mm, 31 faces (baked)
FEATURE [Part::Feature] Part__Feature125  label="MINI USB CONTACT002"
  Placement = pos=(0,0,5.7) rot=(0,1,0;3.14159rad)
  shape: bbox 0.5011 x 2.551 x 9.423 mm, 31 faces (baked)
FEATURE [Part::Feature] Part__Feature126  label="MINI USB CONTACT003"
  Placement = pos=(0.8,0,5.7) rot=(0,1,0;3.14159rad)
  shape: bbox 0.5011 x 2.551 x 9.423 mm, 31 faces (baked)
FEATURE [Part::Feature] Part__Feature127  label="MINI USB CONTACT004"
  Placement = pos=(1.6,0,5.7) rot=(0,1,0;3.14159rad)
  shape: bbox 0.5011 x 2.551 x 9.423 mm, 31 faces (baked)
FEATURE [App::Part] MINIUSB___MEASURED  label="MINIUSB - MEASURED"
  Group = -> [Part__Feature121,Part__Feature122,Part__Feature123,Part__Feature124,Part__Feature125,Part__Feature126,Part__Feature127]
  Origin = -> Origin041
  Placement = pos=(38.98,1.65,-7.62) rot=(0,-1,0;1.5708rad)
FEATURE [Part::Feature] Part__Feature128  label="cap106C"
  Placement = pos=(37.2,-1e-16,-3.3) rot=(0.707107,0,0.707107;3.14159rad)
  shape: bbox 4.001 x 1.811 x 1.701 mm, 124 faces (baked)
FEATURE [Part::Feature] Part__Feature129  label="cap106C001"
  Placement = pos=(7.9,-7e-16,-5.6) rot=(0.707107,0,-0.707107;3.14159rad)
  shape: bbox 4.001 x 1.811 x 1.701 mm, 124 faces (baked)
FEATURE [Part::Feature] Part__Feature130  label="reset core"
  shape: bbox 5.2 x 2.15 x 2.8 mm, 77 faces (baked)
FEATURE [Part::Feature] Part__Feature131  label="reset shell"
  Placement = pos=(0,1.65,0) rot=(0,-1,0;1.5708rad)
  shape: bbox 4 x 1.65 x 3 mm, 100 faces (baked)
FEATURE [App::Part] reset_button  label="reset button"
  Group = -> [Part__Feature130,Part__Feature131]
  Origin = -> Origin042
  Placement = pos=(15.25,1.6,-8.05) rot=(0,1,0;1.5708rad)
FEATURE [Part::Feature] Part__Feature132  label="nano - reg"
  Placement = pos=(6.1,0,-10.16) rot=(0.707107,0,-0.707107;3.14159rad)
  shape: bbox 8.3 x 1.689 x 6.5 mm, 198 faces (baked)
FEATURE [Part::Feature] Part__Feature133  label="NANO DIODE"
  Placement = pos=(11.43,0,-4.2) rot=(0.707107,0,0.707107;3.14159rad)
  shape: bbox 1.7 x 1.384 x 4.916 mm, 85 faces (baked)
FEATURE [Part::Feature] Part__Feature134  label="189 RESISTOR PACK"
  Placement = pos=(15.75,0,-10.85) rot=(0.707107,0,0.707107;3.14159rad)
  shape: bbox 1.3 x 0.3 x 3.2 mm, 21 faces (baked)
FEATURE [Part::Feature] Part__Feature135  label="189 RESISTOR PACK001"
  Placement = pos=(15.75,0,-10.85) rot=(0.707107,0,0.707107;3.14159rad)
  shape: bbox 1.5 x 0.455 x 3.2 mm, 147 faces (baked)
FEATURE [Part::Feature] Part__Feature136  label="189 RESISTOR PACK002"
  Placement = pos=(15.75,0,-10.85) rot=(0.707107,0,0.707107;3.14159rad)
  shape: bbox 0.9095 x 0.4736 x 0.4001 mm, 15 faces (baked)
FEATURE [Part::Feature] Part__Feature137  label="189 RESISTOR PACK003"
  Placement = pos=(15.75,0,-10.85) rot=(0.707107,0,0.707107;3.14159rad)
  shape: bbox 0.9095 x 0.4736 x 0.4001 mm, 15 faces (baked)
FEATURE [Part::Feature] Part__Feature138  label="189 RESISTOR PACK004"
  Placement = pos=(15.75,0,-10.85) rot=(0.707107,0,0.707107;3.14159rad)
  shape: bbox 0.9095 x 0.4736 x 0.4001 mm, 15 faces (baked)
FEATURE [Part::Feature] Part__Feature139  label="189 RESISTOR PACK005"
  Placement = pos=(15.75,0,-10.85) rot=(0.707107,0,0.707107;3.14159rad)
  shape: bbox 0.9095 x 0.4736 x 0.4001 mm, 15 faces (baked)
FEATURE [Part::Feature] Part__Feature140  label="189 RESISTOR PACK006"
  Placement = pos=(15.75,0,-10.85) rot=(0.707107,0,0.707107;3.14159rad)
  shape: bbox 0.9095 x 0.4736 x 0.4001 mm, 15 faces (baked)
FEATURE [Part::Feature] Part__Feature141  label="189 RESISTOR PACK007"
  Placement = pos=(15.75,0,-10.85) rot=(0.707107,0,0.707107;3.14159rad)
  shape: bbox 0.9095 x 0.4736 x 0.4001 mm, 15 faces (baked)
FEATURE [Part::Feature] Part__Feature142  label="189 RESISTOR PACK008"
  Placement = pos=(15.75,0,-10.85) rot=(0.707107,0,0.707107;3.14159rad)
  shape: bbox 0.9095 x 0.4736 x 0.4001 mm, 15 faces (baked)
FEATURE [Part::Feature] Part__Feature143  label="189 RESISTOR PACK009"
  Placement = pos=(15.75,0,-10.85) rot=(0.707107,0,0.707107;3.14159rad)
  shape: bbox 0.9095 x 0.4736 x 0.4001 mm, 15 faces (baked)
FEATURE [App::Part] _89_RESISTOR_PACK  label="189 RESISTOR PACK010"
  Group = -> [Part__Feature134,Part__Feature135,Part__Feature136,Part__Feature137,Part__Feature138,Part__Feature139,Part__Feature140,Part__Feature141,Part__Feature142,Part__Feature143]
  Origin = -> Origin043
FEATURE [Part::Feature] Part__Feature144  label="102 RESISTOR PACK"
  Placement = pos=(15.75,0,-5.2) rot=(0.707107,0,0.707107;3.14159rad)
  shape: bbox 1.3 x 0.3 x 3.2 mm, 21 faces (baked)
FEATURE [Part::Feature] Part__Feature145  label="102 RESISTOR PACK001"
  Placement = pos=(15.75,0,-5.2) rot=(0.707107,0,0.707107;3.14159rad)
  shape: bbox 1.5 x 0.455 x 3.2 mm, 136 faces (baked)
FEATURE [Part::Feature] Part__Feature146  label="102 RESISTOR PACK002"
  Placement = pos=(15.75,0,-5.2) rot=(0.707107,0,0.707107;3.14159rad)
  shape: bbox 0.9095 x 0.4736 x 0.4001 mm, 15 faces (baked)
FEATURE [Part::Feature] Part__Feature147  label="102 RESISTOR PACK003"
  Placement = pos=(15.75,0,-5.2) rot=(0.707107,0,0.707107;3.14159rad)
  shape: bbox 0.9095 x 0.4736 x 0.4001 mm, 15 faces (baked)
FEATURE [Part::Feature] Part__Feature148  label="102 RESISTOR PACK004"
  Placement = pos=(15.75,0,-5.2) rot=(0.707107,0,0.707107;3.14159rad)
  shape: bbox 0.9095 x 0.4736 x 0.4001 mm, 15 faces (baked)
FEATURE [Part::Feature] Part__Feature149  label="102 RESISTOR PACK005"
  Placement = pos=(15.75,0,-5.2) rot=(0.707107,0,0.707107;3.14159rad)
  shape: bbox 0.9095 x 0.4736 x 0.4001 mm, 15 faces (baked)
FEATURE [Part::Feature] Part__Feature150  label="102 RESISTOR PACK006"
  Placement = pos=(15.75,0,-5.2) rot=(0.707107,0,0.707107;3.14159rad)
  shape: bbox 0.9095 x 0.4736 x 0.4001 mm, 15 faces (baked)
FEATURE [Part::Feature] Part__Feature151  label="102 RESISTOR PACK007"
  Placement = pos=(15.75,0,-5.2) rot=(0.707107,0,0.707107;3.14159rad)
  shape: bbox 0.9095 x 0.4736 x 0.4001 mm, 15 faces (baked)
FEATURE [Part::Feature] Part__Feature152  label="102 RESISTOR PACK008"
  Placement = pos=(15.75,0,-5.2) rot=(0.707107,0,0.707107;3.14159rad)
  shape: bbox 0.9095 x 0.4736 x 0.4001 mm, 15 faces (baked)
FEATURE [Part::Feature] Part__Feature153  label="102 RESISTOR PACK009"
  Placement = pos=(15.75,0,-5.2) rot=(0.707107,0,0.707107;3.14159rad)
  shape: bbox 0.9095 x 0.4736 x 0.4001 mm, 15 faces (baked)
FEATURE [App::Part] _02_RESISTOR_PACK  label="102 RESISTOR PACK010"
  Group = -> [Part__Feature144,Part__Feature145,Part__Feature146,Part__Feature147,Part__Feature148,Part__Feature149,Part__Feature150,Part__Feature151,Part__Feature152,Part__Feature153]
  Origin = -> Origin044
FEATURE [App::Part] Arduino_Nano
  Group = -> [Part__Feature099,Part__Feature100,Part__Feature101,Part__Feature102,Part__Feature103,Part__Feature104,Part__Feature105,Part__Feature106,Part__Feature107,Part__Feature108,Part__Feature109,Part__Feature110,Part__Feature111,led,led001,led002,led003,Part__Feature120,MINIUSB___MEASURED,Part__Feature128,Part__Feature129,reset_button,Part__Feature132,Part__Feature133,_89_RESISTOR_PACK,_02_RESISTOR_PACK]
  Origin = -> Origin045
  Placement = pos=(27.7303,49.3507,3) rot=(0.57735,0.57735,0.57735;2.0944rad)
FEATURE [App::Part] U1
  Group = -> [Arduino_Nano]
  Origin = -> Origin046
FEATURE [Part::Feature] Part__Feature154  label="TE-5749181-1"
  Placement = pos=(33.9529,0.00197796,6.5) rot=(1,0,0;1.5708rad)
  shape: bbox 14.03 x 12.83 x 16.56 mm, 256 faces (baked)
FEATURE [App::Part] J2
  Group = -> [Part__Feature154]
  Origin = -> Origin047
FEATURE [Part::Feature] Part__Feature155  label="TE-5749181-002"
  Placement = pos=(15.9529,0.00197796,6.5) rot=(1,0,0;1.5708rad)
  shape: bbox 14.03 x 12.83 x 16.56 mm, 256 faces (baked)
FEATURE [App::Part] J1
  Group = -> [Part__Feature155]
  Origin = -> Origin048
FEATURE [App::Part] PCB
  Group = -> [Board,R4,C2,R3,C1,C7,D3,R8,R7,R6,R5,C5,C4,C3,C6,SW2,SW1,R1,R2,U2,U1,J2,J1]
  Origin = -> Origin049
  Placement = pos=(-26.5,-44.5,10.411) rot=(0,0,1;0rad)
FEATURE [Mesh::Feature] U_Box_V103
FEATURE [Sketcher::SketchObject] Sketch
  ArcFitTolerance = 0
  AttachmentSupport = -> [XY_Plane050]
  FullyConstrained = true
  MakeInternals = false
  MapMode = 5
  sketch-geometry (4):
    g0: LineSegment StartX=-35 StartY=51 StartZ=0 EndX=-35 EndY=-51 EndZ=0
    g1: LineSegment StartX=-35 StartY=-51 StartZ=0 EndX=35 EndY=-51 EndZ=0
    g2: LineSegment StartX=35 StartY=-51 StartZ=0 EndX=35 EndY=51 EndZ=0
    g3: LineSegment StartX=35 StartY=51 StartZ=0 EndX=-35 EndY=51 EndZ=0
  constraints (10):
    c: Coincident(g0,g1)
    c: Coincident(g1,g2)
    c: Coincident(g2,g3)
    c: Coincident(g3,g0)
    c: Vertical(g2)
    c: Horizontal(g3)
    c: Distance(g0,g2) = 70
    c: Distance(g1,g3) = 102
    c: Symmetric(g1,g0,g-2)
    c: Symmetric(g0,g0,g-1)
FEATURE [PartDesign::Pad] Pad
  Direction = (0,0,1)
  Length = 20
  Length2 = 10
  Profile = -> Sketch
  ReferenceAxis = -> Sketch [N_Axis]
  Refine = true
  Suppressed = false
  Type = 0
FEATURE [Sketcher::SketchObject] Sketch001
  ArcFitTolerance = 0
  AttachmentSupport = -> [Pad]
  FullyConstrained = true
  MakeInternals = false
  MapMode = 5
  Placement = pos=(0,0,20) rot=(0,0,1;0rad)
  sketch-geometry (4):
    g0: LineSegment StartX=-32.5 StartY=45 StartZ=0 EndX=-32.5 EndY=-45 EndZ=0
    g1: LineSegment StartX=-32.5 StartY=-45 StartZ=0 EndX=32.5 EndY=-45 EndZ=0
    g2: LineSegment StartX=32.5 StartY=-45 StartZ=0 EndX=32.5 EndY=45 EndZ=0
    g3: LineSegment StartX=32.5 StartY=45 StartZ=0 EndX=-32.5 EndY=45 EndZ=0
  constraints (10):
    c: Coincident(g0,g1)
    c: Coincident(g1,g2)
    c: Coincident(g2,g3)
    c: Coincident(g3,g0)
    c: Vertical(g2)
    c: Horizontal(g1)
    c: Symmetric(g0,g2,g-2)
    c: Symmetric(g0,g0,g-1)
    c: DistanceX(g3,g3) = 65
    c: DistanceY(g2,g2) = 90
FEATURE [PartDesign::Pocket] Pocket
  BaseFeature = -> Pad
  Direction = (0,0,-1)
  Length = 18
  Length2 = 5
  Profile = -> Sketch001
  ReferenceAxis = -> Sketch001 [N_Axis]
  Refine = true
  Suppressed = false
  Type = 0
FEATURE [Sketcher::SketchObject] Sketch002
  ArcFitTolerance = 0
  AttachmentSupport = -> [Pocket]
  ExternalGeometry = -> [Pocket]
  FullyConstrained = true
  MakeInternals = false
  MapMode = 5
  Placement = pos=(0,51,0) rot=(0,0.707107,0.707107;3.14159rad)
  sketch-geometry (4):
    g0: LineSegment StartX=-31 StartY=20 StartZ=0 EndX=-31 EndY=4 EndZ=0
    g1: LineSegment StartX=-31 StartY=4 StartZ=0 EndX=31 EndY=4 EndZ=0
    g2: LineSegment StartX=31 StartY=4 StartZ=0 EndX=31 EndY=20 EndZ=0
    g3: LineSegment StartX=31 StartY=20 StartZ=0 EndX=-31 EndY=20 EndZ=0
  constraints (11):
    c: Coincident(g0,g1)
    c: Coincident(g1,g2)
    c: Coincident(g2,g3)
    c: Coincident(g3,g0)
    c: Vertical(g0)
    c: Vertical(g2)
    c: Horizontal(g1)
    c: PointOnObject(g0,g-3)
    c: Symmetric(g2,g0,g-2)
    c: DistanceY(g-1,g0) = 4
    c: Distance(g-3,g0) = 4
FEATURE [PartDesign::Pocket] Pocket001
  BaseFeature = -> Pocket
  Direction = (0,-1,2e-16)
  Length = 5
  Length2 = 5
  Profile = -> Sketch002
  ReferenceAxis = -> Sketch002 [N_Axis]
  Refine = true
  Suppressed = false
  Type = 1
FEATURE [Sketcher::SketchObject] Sketch003
  ArcFitTolerance = 0
  AttachmentSupport = -> [Pocket001]
  ExternalGeometry = -> [Pocket001]
  FullyConstrained = true
  MakeInternals = false
  MapMode = 5
  Placement = pos=(0,51,0) rot=(0,0.707107,0.707107;3.14159rad)
  sketch-geometry (4):
    g0: LineSegment StartX=-33 StartY=20 StartZ=0 EndX=-33 EndY=2 EndZ=0
    g1: LineSegment StartX=-33 StartY=2 StartZ=0 EndX=33 EndY=2 EndZ=0
    g2: LineSegment StartX=33 StartY=2 StartZ=0 EndX=33 EndY=20 EndZ=0
    g3: LineSegment StartX=33 StartY=20 StartZ=0 EndX=-33 EndY=20 EndZ=0
  constraints (11):
    c: Coincident(g0,g1)
    c: Coincident(g1,g2)
    c: Coincident(g2,g3)
    c: Coincident(g3,g0)
    c: Vertical(g0)
    c: Vertical(g2)
    c: Horizontal(g1)
    c: Symmetric(g0,g2,g-2)
    c: DistanceX(g-3,g0) = 2
    c: PointOnObject(g0,g-3)
    c: Distance(g0,g-1) = 2
FEATURE [PartDesign::Pocket] Pocket002
  BaseFeature = -> Pocket001
  Direction = (0,-1,2e-16)
  Length = 4
  Length2 = -2
  Profile = -> Sketch003
  ReferenceAxis = -> Sketch003 [N_Axis]
  Refine = true
  Suppressed = false
  Type = 4
FEATURE [PartDesign::Mirrored] Mirrored
  BaseFeature = -> Pocket002
  MirrorPlane = -> XZ_Plane050
  Originals = -> [Pocket002]
  Refine = true
  Suppressed = false
  TransformMode = 0
FEATURE [Sketcher::SketchObject] Sketch004
  ArcFitTolerance = 0
  AttachmentSupport = -> [Mirrored]
  FullyConstrained = true
  MakeInternals = false
  MapMode = 5
  Placement = pos=(0,0,2) rot=(0,0,1;0rad)
  sketch-geometry (8):
    g0: Circle CenterX=-21.5 CenterY=39.5 CenterZ=0 NormalX=0 NormalY=0 NormalZ=1 AngleXU=0 Radius=3
    g1: Circle CenterX=21.5 CenterY=39.5 CenterZ=0 NormalX=0 NormalY=0 NormalZ=1 AngleXU=0 Radius=3
    g2: Circle CenterX=-21.5 CenterY=-39.5 CenterZ=0 NormalX=0 NormalY=0 NormalZ=1 AngleXU=0 Radius=3
    g3: Circle CenterX=21.5 CenterY=-39.5 CenterZ=0 NormalX=0 NormalY=0 NormalZ=1 AngleXU=0 Radius=3
    g4: Circle CenterX=-21.5 CenterY=39.5 CenterZ=0 NormalX=0 NormalY=0 NormalZ=1 AngleXU=0 Radius=1.25
    g5: Circle CenterX=21.5 CenterY=39.5 CenterZ=0 NormalX=0 NormalY=0 NormalZ=1 AngleXU=0 Radius=1.25
    g6: Circle CenterX=-21.5 CenterY=-39.5 CenterZ=0 NormalX=0 NormalY=0 NormalZ=1 AngleXU=0 Radius=1.25
    g7: Circle CenterX=21.5 CenterY=-39.5 CenterZ=0 NormalX=0 NormalY=0 NormalZ=1 AngleXU=0 Radius=1.25
  constraints (17):
    c: Equal(g0,g1)
    c: Equal(g1,g2)
    c: Equal(g2,g3)
    c: Symmetric(g2,g3,g-2)
    c: Symmetric(g0,g1,g-2)
    c: Symmetric(g0,g2,g-1)
    c: DistanceY(g2,g0) = 79
    c: DistanceX(g0,g1) = 43
    c: Diameter(g0) = 6
    c: Coincident(g4,g0)
    c: Coincident(g5,g1)
    c: Coincident(g6,g2)
    c: Coincident(g7,g3)
    c: Equal(g5,g4)
    c: Equal(g4,g6)
    c: Equal(g6,g7)
    c: Diameter(g4) = 2.5
FEATURE [PartDesign::Pad] Pad001
  BaseFeature = -> Mirrored
  Direction = (0,0,1)
  Length = 8
  Length2 = 10
  Profile = -> Sketch004
  ReferenceAxis = -> Sketch004 [N_Axis]
  Refine = true
  Suppressed = false
  Type = 0
FEATURE [PartDesign::Chamfer] Chamfer
  Angle = 45
  Base = -> Pad001 [Edge98,Edge97,Edge99,Edge100]
  BaseFeature = -> Pad001
  ChamferType = 0
  FlipDirection = false
  Refine = true
  Size = 2
  Size2 = 1
  SupportTransform = false
  Suppressed = false
  UseAllEdges = false
FEATURE [PartDesign::Fillet] Fillet
  Base = -> Chamfer [Edge106,Edge103,Edge112,Edge107,Edge19,Edge11,Edge25,Edge12]
  BaseFeature = -> Chamfer
  Radius = 1
  Refine = true
  SupportTransform = false
  Suppressed = false
  UseAllEdges = false
FEATURE [PartDesign::Chamfer] Chamfer001
  Angle = 45
  Base = -> Fillet [Face53]
  BaseFeature = -> Fillet
  ChamferType = 0
  FlipDirection = false
  Refine = true
  Size = 2
  Size2 = 1
  SupportTransform = false
  Suppressed = false
  UseAllEdges = false
FEATURE [PartDesign::Fillet] Fillet001
  Base = -> Chamfer001 [Edge112]
  BaseFeature = -> Chamfer001
  Radius = 1
  Refine = true
  SupportTransform = false
  Suppressed = false
  UseAllEdges = false
FEATURE [Sketcher::SketchObject] Sketch005
  ArcFitTolerance = 0
  AttachmentSupport = -> [Fillet001]
  ExternalGeometry = -> [Fillet001]
  FullyConstrained = true
  MakeInternals = false
  MapMode = 5
  Placement = pos=(0,0,20) rot=(0,0,1;0rad)
  sketch-geometry (4):
    g0: LineSegment StartX=31.75 StartY=40 StartZ=0 EndX=31.75 EndY=-40 EndZ=0
    g1: LineSegment StartX=31.75 StartY=-40 StartZ=0 EndX=30.75 EndY=-40 EndZ=0
    g2: LineSegment StartX=30.75 StartY=-40 StartZ=0 EndX=30.75 EndY=40 EndZ=0
    g3: LineSegment StartX=30.75 StartY=40 StartZ=0 EndX=31.75 EndY=40 EndZ=0
  constraints (11):
    c: Coincident(g0,g1)
    c: Coincident(g1,g2)
    c: Coincident(g2,g3)
    c: Coincident(g3,g0)
    c: Vertical(g2)
    c: Horizontal(g1)
    c: Horizontal(g3)
    c: Distance(g0,g2) = 1
    c: Distance(g1,g3) = 80
    c: Symmetric(g0,g0,g-1)
    c: DistanceX(g-3,g0) = 0.75
FEATURE [PartDesign::Pocket] Pocket003
  BaseFeature = -> Fillet001
  Direction = (0,0,-1)
  Length = 1
  Length2 = 5
  Profile = -> Sketch005
  ReferenceAxis = -> Sketch005 [N_Axis]
  Refine = true
  Suppressed = false
  Type = 0
FEATURE [PartDesign::Mirrored] Mirrored001
  BaseFeature = -> Pocket003
  MirrorPlane = -> Sketch005 [V_Axis]
  Originals = -> [Pocket003]
  Refine = true
  Suppressed = false
  TransformMode = 0
FEATURE [Sketcher::SketchObject] Sketch006
  ArcFitTolerance = 0
  AttachmentSupport = -> [Mirrored001]
  ExternalGeometry = -> [Mirrored001]
  FullyConstrained = true
  MakeInternals = false
  MapMode = 5
  Placement = pos=(35,0,0) rot=(0.57735,0.57735,0.57735;2.0944rad)
  sketch-geometry (2):
    g0: Circle CenterX=-30 CenterY=16 CenterZ=0 NormalX=0 NormalY=0 NormalZ=1 AngleXU=0 Radius=1.25
    g1: Circle CenterX=30 CenterY=16 CenterZ=0 NormalX=0 NormalY=0 NormalZ=1 AngleXU=0 Radius=1.25
  constraints (5):
    c: Equal(g1,g0)
    c: Symmetric(g0,g1,g-2)
    c: DistanceX(g0,g1) = 60
    c: Diameter(g0) = 2.5
    c: DistanceY(g-1,g1) = 16
FEATURE [PartDesign::Pocket] Pocket004
  BaseFeature = -> Mirrored001
  Direction = (-1,0,0)
  Length = 5
  Length2 = 5
  Profile = -> Sketch006
  ReferenceAxis = -> Sketch006 [N_Axis]
  Refine = true
  Suppressed = false
  Type = 1
FEATURE [PartDesign::Mirrored] Mirrored002
  BaseFeature = -> Pocket004
  MirrorPlane = -> YZ_Plane050
  Originals = -> [Pocket004]
  Refine = true
  Suppressed = false
  TransformMode = 0
FEATURE [PartDesign::Body] Body  label="Bottom"
  AllowCompound = false
  Group = -> [Sketch,Pad,Sketch001,Pocket,Sketch002,Pocket001,Sketch003,Pocket002,Mirrored,Sketch004,Pad001,Chamfer,Fillet,Chamfer001,Fillet001,Sketch005,Pocket003,Mirrored001,Sketch006,Pocket004,Mirrored002]
  Origin = -> Origin050
  Tip = -> Mirrored002
FEATURE [PartDesign::Plane] DatumPlane
  AttachmentSupport = -> [Mirrored002]
  Length = 77.6965
  MapMode = 5
  Placement = pos=(0,-45,0) rot=(0,0.707107,0.707107;3.14159rad)
  ResizeMode = 0
  Width = 74.6965
FEATURE [Sketcher::SketchObject] Sketch007
  ArcFitTolerance = 0
  AttachmentSupport = -> [DatumPlane]
  FullyConstrained = true
  MakeInternals = false
  MapMode = 5
  Placement = pos=(0,-45,0) rot=(0,0.707107,0.707107;3.14159rad)
  sketch-geometry (4):
    g0: LineSegment StartX=-32.5 StartY=37 StartZ=0 EndX=-32.5 EndY=2 EndZ=0
    g1: LineSegment StartX=-32.5 StartY=2 StartZ=0 EndX=32.5 EndY=2 EndZ=0
    g2: LineSegment StartX=32.5 StartY=2 StartZ=0 EndX=32.5 EndY=37 EndZ=0
    g3: LineSegment StartX=32.5 StartY=37 StartZ=0 EndX=-32.5 EndY=37 EndZ=0
  constraints (11):
    c: Coincident(g0,g1)
    c: Coincident(g1,g2)
    c: Coincident(g2,g3)
    c: Coincident(g3,g0)
    c: Vertical(g0)
    c: Vertical(g2)
    c: Horizontal(g1)
    c: Symmetric(g0,g2,g-2)
    c: DistanceY(g0,g0) = 35
    c: DistanceX(g1,g1) = 65
    c: Distance(g0,g-1) = 2
FEATURE [PartDesign::Pad] Pad002
  Direction = (0,1,-2e-16)
  Length = 1.5
  Length2 = 10
  Placement = pos=(0,-45,0) rot=(0,0.707107,0.707107;3.14159rad)
  Profile = -> Sketch007
  ReferenceAxis = -> Sketch007 [N_Axis]
  Refine = true
  Suppressed = false
  Type = 0
FEATURE [Sketcher::SketchObject] Sketch008
  ArcFitTolerance = 0
  AttachmentSupport = -> [Pad002]
  FullyConstrained = true
  MakeInternals = false
  MapMode = 5
  Placement = pos=(0,-43.5,0) rot=(0,0.707107,0.707107;3.14159rad)
  sketch-geometry (8):
    g0: LineSegment StartX=-18 StartY=24 StartZ=0 EndX=-18 EndY=10 EndZ=0
    g1: LineSegment StartX=-18 StartY=10 StartZ=0 EndX=-3 EndY=10 EndZ=0
    g2: LineSegment StartX=-3 StartY=10 StartZ=0 EndX=-3 EndY=24 EndZ=0
    g3: LineSegment StartX=-3 StartY=24 StartZ=0 EndX=-18 EndY=24 EndZ=0
    g4: LineSegment StartX=0 StartY=10 StartZ=0 EndX=15 EndY=10 EndZ=0
    g5: LineSegment StartX=15 StartY=10 StartZ=0 EndX=15 EndY=24 EndZ=0
    g6: LineSegment StartX=15 StartY=24 StartZ=0 EndX=0 EndY=24 EndZ=0
    g7: LineSegment StartX=0 StartY=24 StartZ=0 EndX=0 EndY=10 EndZ=0
  constraints (24):
    c: Coincident(g0,g1)
    c: Coincident(g1,g2)
    c: Coincident(g2,g3)
    c: Coincident(g3,g0)
    c: Vertical(g0)
    c: Vertical(g2)
    c: Horizontal(g1)
    c: Horizontal(g3)
    c: Coincident(g4,g5)
    c: Coincident(g5,g6)
    c: Coincident(g6,g7)
    c: Coincident(g7,g4)
    c: Horizontal(g4)
    c: Horizontal(g6)
    c: Vertical(g5)
    c: Vertical(g7)
    c: Equal(g3,g6)
    c: Equal(g0,g7)
    c: Horizontal(g0,g4)
    c: DistanceY(g0,g0) = 14
    c: DistanceX(g3,g3) = 15
    c: DistanceY(g-1,g0) = 10
    c: DistanceX(g0,g-1) = 18
    c: DistanceX(g2,g6) = 3
FEATURE [PartDesign::Pocket] Pocket005
  BaseFeature = -> Pad002
  Direction = (0,-1,2e-16)
  Length = 5
  Length2 = 5
  Placement = pos=(0,-45,0) rot=(0,0.707107,0.707107;3.14159rad)
  Profile = -> Sketch008
  ReferenceAxis = -> Sketch008 [N_Axis]
  Refine = true
  Suppressed = false
  Type = 1
FEATURE [PartDesign::Fillet] Fillet002
  Base = -> Pocket005 [Edge1,Edge2,Edge8,Edge5,Edge36,Edge33,Edge35,Edge34,Edge31,Edge30,Edge32,Edge29]
  BaseFeature = -> Pocket005
  Placement = pos=(0,-45,0) rot=(0,0.707107,0.707107;3.14159rad)
  Radius = 2
  Refine = true
  SupportTransform = false
  Suppressed = false
  UseAllEdges = false
FEATURE [Sketcher::SketchObject] Sketch009
  ArcFitTolerance = 0
  AttachmentSupport = -> [Fillet002]
  FullyConstrained = true
  MakeInternals = false
  MapMode = 5
  Placement = pos=(0,-43.5,0) rot=(0,0.707107,0.707107;3.14159rad)
FEATURE [PartDesign::Body] Body001  label="Front"
  AllowCompound = false
  Group = -> [DatumPlane,Sketch007,Pad002,Sketch008,Pocket005,Fillet002,Sketch009]
  Origin = -> Origin051
  Tip = -> Fillet002
FEATURE [PartDesign::Plane] DatumPlane001
  AttachmentSupport = -> [Mirrored002]
  Length = 77.6965
  MapMode = 5
  Placement = pos=(0,-47,-3.95e-14) rot=(1,0,0;1.5708rad)
  ResizeMode = 0
  Width = 74.6965
FEATURE [Sketcher::SketchObject] Sketch010
  ArcFitTolerance = 0
  AttachmentSupport = -> [DatumPlane001]
  FullyConstrained = true
  MakeInternals = false
  MapMode = 5
  Placement = pos=(0,-47,-3.95e-14) rot=(1,0,0;1.5708rad)
  sketch-geometry (8):
    g0: LineSegment StartX=-32.5 StartY=37 StartZ=0 EndX=-32.5 EndY=2 EndZ=0
    g1: LineSegment StartX=-32.5 StartY=2 StartZ=0 EndX=32.5 EndY=2 EndZ=0
    g2: LineSegment StartX=32.5 StartY=2 StartZ=0 EndX=32.5 EndY=37 EndZ=0
    g3: LineSegment StartX=32.5 StartY=37 StartZ=0 EndX=-32.5 EndY=37 EndZ=0
    g4: LineSegment StartX=0 StartY=29 StartZ=0 EndX=0 EndY=19 EndZ=0
    g5: LineSegment StartX=0 StartY=19 StartZ=0 EndX=13 EndY=19 EndZ=0
    g6: LineSegment StartX=13 StartY=19 StartZ=0 EndX=13 EndY=29 EndZ=0
    g7: LineSegment StartX=13 StartY=29 StartZ=0 EndX=0 EndY=29 EndZ=0
  constraints (23):
    c: Coincident(g0,g1)
    c: Coincident(g1,g2)
    c: Coincident(g2,g3)
    c: Coincident(g3,g0)
    c: Vertical(g0)
    c: Vertical(g2)
    c: Horizontal(g1)
    c: Symmetric(g0,g2,g-2)
    c: DistanceY(g-1,g0) = 2
    c: DistanceX(g3,g3) = 65
    c: DistanceY(g0,g0) = 35
    c: Coincident(g4,g5)
    c: Coincident(g5,g6)
    c: Coincident(g6,g7)
    c: Coincident(g7,g4)
    c: Vertical(g4)
    c: Vertical(g6)
    c: Horizontal(g5)
    c: Horizontal(g7)
    c: DistanceX(g7,g7) = 13
    c: DistanceY(g6,g6) = 10
    c: DistanceY(g-1,g4) = 19
    c: PointOnObject(g4,g-2)
FEATURE [PartDesign::Pad] Pad003
  Direction = (0,-1,2e-16)
  Length = 1.5
  Length2 = 10
  Placement = pos=(0,-47,-3.94e-14) rot=(1,0,0;1.5708rad)
  Profile = -> Sketch010
  ReferenceAxis = -> Sketch010 [N_Axis]
  Refine = true
  Suppressed = false
  Type = 0
FEATURE [PartDesign::Fillet] Fillet003
  Base = -> Pad003 [Edge1,Edge8,Edge5,Edge2,Edge13,Edge20,Edge14,Edge17]
  BaseFeature = -> Pad003
  Placement = pos=(0,-47,-3.94e-14) rot=(1,0,0;1.5708rad)
  Radius = 2
  Refine = true
  SupportTransform = false
  Suppressed = false
  UseAllEdges = false
FEATURE [Sketcher::SketchObject] Sketch011
  ArcFitTolerance = 0
  AttachmentSupport = -> [XY_Plane053]
  FullyConstrained = true
  MakeInternals = false
  MapMode = 5
  sketch-geometry (4):
    g0: LineSegment StartX=-35 StartY=51 StartZ=0 EndX=-35 EndY=-51 EndZ=0
    g1: LineSegment StartX=-35 StartY=-51 StartZ=0 EndX=35 EndY=-51 EndZ=0
    g2: LineSegment StartX=35 StartY=-51 StartZ=0 EndX=35 EndY=51 EndZ=0
    g3: LineSegment StartX=35 StartY=51 StartZ=0 EndX=-35 EndY=51 EndZ=0
  constraints (10):
    c: Coincident(g0,g1)
    c: Coincident(g1,g2)
    c: Coincident(g2,g3)
    c: Coincident(g3,g0)
    c: Vertical(g2)
    c: Horizontal(g3)
    c: Distance(g0,g2) = 70
    c: Distance(g1,g3) = 102
    c: Symmetric(g1,g0,g-2)
    c: Symmetric(g0,g0,g-1)
FEATURE [PartDesign::Pad] Pad004
  Direction = (0,0,1)
  Length = 20
  Length2 = 10
  Profile = -> Sketch011
  ReferenceAxis = -> Sketch011 [N_Axis]
  Refine = true
  Suppressed = false
  Type = 0
FEATURE [Sketcher::SketchObject] Sketch012
  ArcFitTolerance = 0
  AttachmentSupport = -> [Pad004]
  FullyConstrained = true
  MakeInternals = false
  MapMode = 5
  Placement = pos=(0,0,20) rot=(0,0,1;0rad)
  sketch-geometry (4):
    g0: LineSegment StartX=-32.5 StartY=45 StartZ=0 EndX=-32.5 EndY=-45 EndZ=0
    g1: LineSegment StartX=-32.5 StartY=-45 StartZ=0 EndX=32.5 EndY=-45 EndZ=0
    g2: LineSegment StartX=32.5 StartY=-45 StartZ=0 EndX=32.5 EndY=45 EndZ=0
    g3: LineSegment StartX=32.5 StartY=45 StartZ=0 EndX=-32.5 EndY=45 EndZ=0
  constraints (10):
    c: Coincident(g0,g1)
    c: Coincident(g1,g2)
    c: Coincident(g2,g3)
    c: Coincident(g3,g0)
    c: Vertical(g2)
    c: Horizontal(g1)
    c: Symmetric(g0,g2,g-2)
    c: Symmetric(g0,g0,g-1)
    c: DistanceX(g3,g3) = 65
    c: DistanceY(g2,g2) = 90
FEATURE [PartDesign::Pocket] Pocket006
  BaseFeature = -> Pad004
  Direction = (0,0,-1)
  Length = 18
  Length2 = 5
  Profile = -> Sketch012
  ReferenceAxis = -> Sketch012 [N_Axis]
  Refine = true
  Suppressed = false
  Type = 0
FEATURE [Sketcher::SketchObject] Sketch013
  ArcFitTolerance = 0
  AttachmentSupport = -> [Pocket006]
  ExternalGeometry = -> [Pocket006]
  FullyConstrained = true
  MakeInternals = false
  MapMode = 5
  Placement = pos=(0,51,0) rot=(0,0.707107,0.707107;3.14159rad)
  sketch-geometry (4):
    g0: LineSegment StartX=-31 StartY=20 StartZ=0 EndX=-31 EndY=4 EndZ=0
    g1: LineSegment StartX=-31 StartY=4 StartZ=0 EndX=31 EndY=4 EndZ=0
    g2: LineSegment StartX=31 StartY=4 StartZ=0 EndX=31 EndY=20 EndZ=0
    g3: LineSegment StartX=31 StartY=20 StartZ=0 EndX=-31 EndY=20 EndZ=0
  constraints (11):
    c: Coincident(g0,g1)
    c: Coincident(g1,g2)
    c: Coincident(g2,g3)
    c: Coincident(g3,g0)
    c: Vertical(g0)
    c: Vertical(g2)
    c: Horizontal(g1)
    c: PointOnObject(g0,g-3)
    c: Symmetric(g2,g0,g-2)
    c: DistanceY(g-1,g0) = 4
    c: Distance(g-3,g0) = 4
FEATURE [PartDesign::Pocket] Pocket007
  BaseFeature = -> Pocket006
  Direction = (0,-1,2e-16)
  Length = 5
  Length2 = 5
  Profile = -> Sketch013
  ReferenceAxis = -> Sketch013 [N_Axis]
  Refine = true
  Suppressed = false
  Type = 1
FEATURE [Sketcher::SketchObject] Sketch014
  ArcFitTolerance = 0
  AttachmentSupport = -> [Pocket007]
  ExternalGeometry = -> [Pocket007]
  FullyConstrained = true
  MakeInternals = false
  MapMode = 5
  Placement = pos=(0,51,0) rot=(0,0.707107,0.707107;3.14159rad)
  sketch-geometry (4):
    g0: LineSegment StartX=-33 StartY=20 StartZ=0 EndX=-33 EndY=2 EndZ=0
    g1: LineSegment StartX=-33 StartY=2 StartZ=0 EndX=33 EndY=2 EndZ=0
    g2: LineSegment StartX=33 StartY=2 StartZ=0 EndX=33 EndY=20 EndZ=0
    g3: LineSegment StartX=33 StartY=20 StartZ=0 EndX=-33 EndY=20 EndZ=0
  constraints (11):
    c: Coincident(g0,g1)
    c: Coincident(g1,g2)
    c: Coincident(g2,g3)
    c: Coincident(g3,g0)
    c: Vertical(g0)
    c: Vertical(g2)
    c: Horizontal(g1)
    c: Symmetric(g0,g2,g-2)
    c: DistanceX(g-3,g0) = 2
    c: PointOnObject(g0,g-3)
    c: Distance(g0,g-1) = 2
FEATURE [PartDesign::Pocket] Pocket008
  BaseFeature = -> Pocket007
  Direction = (0,-1,2e-16)
  Length = 4
  Length2 = -2
  Profile = -> Sketch014
  ReferenceAxis = -> Sketch014 [N_Axis]
  Refine = true
  Suppressed = false
  Type = 4
FEATURE [PartDesign::Mirrored] Mirrored003
  BaseFeature = -> Pocket008
  MirrorPlane = -> XZ_Plane053
  Originals = -> [Pocket008]
  Refine = true
  Suppressed = false
  TransformMode = 0
FEATURE [Sketcher::SketchObject] Sketch015
  ArcFitTolerance = 0
  AttachmentSupport = -> [Mirrored003]
  ExternalGeometry = -> [Mirrored003]
  FullyConstrained = true
  MakeInternals = false
  MapMode = 5
  Placement = pos=(0,0,20) rot=(0,0,1;0rad)
  sketch-geometry (4):
    g0: LineSegment StartX=-33.25 StartY=39 StartZ=0 EndX=-34.25 EndY=39 EndZ=0
    g1: LineSegment StartX=-34.25 StartY=39 StartZ=0 EndX=-34.25 EndY=-39 EndZ=0
    g2: LineSegment StartX=-34.25 StartY=-39 StartZ=0 EndX=-33.25 EndY=-39 EndZ=0
    g3: LineSegment StartX=-33.25 StartY=-39 StartZ=0 EndX=-33.25 EndY=39 EndZ=0
  constraints (11):
    c: Coincident(g0,g1)
    c: Coincident(g1,g2)
    c: Coincident(g2,g3)
    c: Coincident(g3,g0)
    c: Horizontal(g0)
    c: Horizontal(g2)
    c: Vertical(g3)
    c: Distance(g0,g0) = 1
    c: DistanceY(g1,g1) = 78
    c: Symmetric(g0,g1,g-1)
    c: Distance(g0,g-3) = 0.75
FEATURE [PartDesign::Pad] Pad005
  BaseFeature = -> Mirrored003
  Direction = (0,0,1)
  Length = 1
  Length2 = 10
  Profile = -> Sketch015
  ReferenceAxis = -> Sketch015 [N_Axis]
  Refine = true
  Suppressed = false
  Type = 0
FEATURE [PartDesign::Mirrored] Mirrored004
  BaseFeature = -> Pad005
  MirrorPlane = -> Sketch015 [V_Axis]
  Originals = -> [Pad005]
  Refine = true
  Suppressed = false
  TransformMode = 0
FEATURE [Sketcher::SketchObject] Sketch016
  ArcFitTolerance = 0
  AttachmentSupport = -> [Mirrored004]
  ExternalGeometry = -> [Mirrored004]
  FullyConstrained = true
  MakeInternals = false
  MapMode = 5
  Placement = pos=(32.5,0,0) rot=(0.57735,-0.57735,-0.57735;2.0944rad)
  sketch-geometry (8):
    g0: LineSegment StartX=-40 StartY=15 StartZ=0 EndX=-20 EndY=15 EndZ=0
    g1: LineSegment StartX=-20 StartY=15 StartZ=0 EndX=-20 EndY=20 EndZ=0
    g2: LineSegment StartX=-20 StartY=20 StartZ=0 EndX=-25 EndY=27 EndZ=0
    g3: LineSegment StartX=-25 StartY=27 StartZ=0 EndX=-35 EndY=27 EndZ=0
    g4: LineSegment StartX=-35 StartY=27 StartZ=0 EndX=-40 EndY=20 EndZ=0
    g5: LineSegment StartX=-40 StartY=20 StartZ=0 EndX=-40 EndY=15 EndZ=0
    g6: Circle CenterX=-30 CenterY=24 CenterZ=0 NormalX=0 NormalY=0 NormalZ=1 AngleXU=0 Radius=1
    g7: GeomPoint X=-30 Y=15 Z=0
  constraints (22):
    c: Coincident(g0,g1)
    c: Vertical(g1)
    c: Coincident(g1,g2)
    c: Coincident(g2,g3)
    c: Coincident(g3,g4)
    c: Coincident(g4,g5)
    c: Coincident(g5,g0)
    c: Vertical(g5)
    c: DistanceX(g0,g0) = 20
    c: DistanceX(g3,g3) = 10
    c: DistanceY(g-1,g0) = 15
    c: DistanceY(g-1,g3) = 27
    c: DistanceY(g5,g5) = 5
    c: Equal(g1,g5)
    c: Diameter(g6) = 2
    c: Distance(g6,g-3) = 4
    c: Equal(g2,g4)
    c: Horizontal(g0)
    c: Horizontal(g3)
    c: Symmetric(g0,g0,g7)
    c: Vertical(g6,g7)
    c: Distance(g7,g-2) = 30
FEATURE [PartDesign::Pad] Pad006
  BaseFeature = -> Mirrored004
  Direction = (-1,0,0)
  Length = 3
  Length2 = 10
  Profile = -> Sketch016
  ReferenceAxis = -> Sketch016 [N_Axis]
  Refine = true
  Suppressed = false
  Type = 0
FEATURE [PartDesign::Mirrored] Mirrored005
  MirrorPlane = -> XZ_Plane053
  Refine = true
  Suppressed = false
  TransformMode = 0
FEATURE [PartDesign::Mirrored] Mirrored006
  MirrorPlane = -> YZ_Plane053
  Refine = true
  Suppressed = false
  TransformMode = 0
FEATURE [PartDesign::MultiTransform] MultiTransform
  BaseFeature = -> Pad006
  Originals = -> [Pad006]
  Refine = true
  Suppressed = false
  TransformMode = 0
  Transformations = -> [Mirrored005,Mirrored006]
FEATURE [Sketcher::SketchObject] Sketch017
  ArcFitTolerance = 0
  AttachmentSupport = -> [MultiTransform]
  FullyConstrained = true
  MakeInternals = false
  MapMode = 5
  Placement = pos=(0,0,0) rot=(1,0,0;3.14159rad)
  sketch-geometry (2):
    g0: Circle CenterX=-7.5 CenterY=25.4 CenterZ=0 NormalX=0 NormalY=0 NormalZ=1 AngleXU=0 Radius=6
    g1: Circle CenterX=10.5 CenterY=25.4 CenterZ=0 NormalX=0 NormalY=0 NormalZ=1 AngleXU=0 Radius=6
  constraints (6):
    c: Equal(g0,g1)
    c: Horizontal(g0,g1)
    c: DistanceX(g0,g1) = 18
    c: DistanceY(g-1,g0) = 25.4
    c: DistanceX(g0,g-1) = 7.5
    c: Diameter(g0) = 12
FEATURE [PartDesign::Pocket] Pocket009
  BaseFeature = -> MultiTransform
  Direction = (0,0,1)
  Length = 5
  Length2 = 5
  Profile = -> Sketch017
  ReferenceAxis = -> Sketch017 [N_Axis]
  Refine = true
  Suppressed = false
  Type = 1
FEATURE [PartDesign::Chamfer] Chamfer002
  Angle = 45
  Base = -> Pocket009 [Edge3,Edge12,Edge19,Edge5]
  BaseFeature = -> Pocket009
  ChamferType = 0
  FlipDirection = false
  Refine = true
  Size = 2
  Size2 = 1
  SupportTransform = false
  Suppressed = false
  UseAllEdges = false
FEATURE [PartDesign::Fillet] Fillet004
  Base = -> Chamfer002 [Edge111,Edge99,Edge110,Edge128,Edge101,Edge149,Edge129,Edge100]
  BaseFeature = -> Chamfer002
  Radius = 1
  Refine = true
  SupportTransform = false
  Suppressed = false
  UseAllEdges = false
FEATURE [PartDesign::Fillet] Fillet005
  Base = -> Fillet004 [Edge79,Edge70,Edge72,Edge86]
  BaseFeature = -> Fillet004
  Radius = 1
  Refine = true
  SupportTransform = false
  Suppressed = false
  UseAllEdges = false
FEATURE [PartDesign::Chamfer] Chamfer003
  Angle = 45
  Base = -> Fillet005 [Edge213,Edge217,Edge94,Edge99]
  BaseFeature = -> Fillet005
  ChamferType = 0
  FlipDirection = false
  Refine = true
  Size = 2.9
  Size2 = 1
  SupportTransform = false
  Suppressed = false
  UseAllEdges = false
FEATURE [Sketcher::SketchObject] Sketch018
  ArcFitTolerance = 0
  AttachmentSupport = -> [YZ_Plane054]
  FullyConstrained = true
  MakeInternals = false
  MapMode = 5
  Placement = pos=(0,0,0) rot=(0.57735,0.57735,0.57735;2.0944rad)
  sketch-geometry (7):
    g0: LineSegment StartX=1.8 StartY=0 StartZ=0 EndX=5.3 EndY=0 EndZ=0
    g1: ArcOfCircle CenterX=0 CenterY=14.9268 CenterZ=0 NormalX=0 NormalY=0 NormalZ=1 AngleXU=0 Radius=5.52324 StartAngle=0.0917729 EndAngle=1.5708
    g2: LineSegment StartX=0 StartY=20.45 StartZ=0 EndX=0 EndY=5 EndZ=0
    g3: LineSegment StartX=1.8 StartY=5 StartZ=0 EndX=1.8 EndY=0 EndZ=0
    g4: LineSegment StartX=0 StartY=5 StartZ=0 EndX=1.8 EndY=5 EndZ=0
    g5: LineSegment StartX=5.5 StartY=15.4329 StartZ=0 EndX=6 EndY=10 EndZ=0
    g6: LineSegment StartX=6 StartY=10 StartZ=0 EndX=5.3 EndY=0 EndZ=0
  constraints (21):
    c: PointOnObject(g0,g-1)
    c: Horizontal(g0)
    c: PointOnObject(g1,g-2)
    c: Coincident(g1,g2)
    c: PointOnObject(g2,g-2)
    c: Coincident(g3,g0)
    c: Coincident(g2,g4)
    c: Horizontal(g4)
    c: Vertical(g3)
    c: Distance(g0,g-2) = 1.8
    c: DistanceX(g-1,g1) = 5.5
    c: DistanceY(g-1,g2) = 5
    c: Coincident(g3,g4)
    c: DistanceY(g2,g1) = 15.45
    c: Coincident(g5,g6)
    c: Coincident(g6,g0)
    c: Distance(g0,g0) = 3.5
    c: Distance(g5,g2) = 6
    c: DistanceY(g-1,g5) = 10
    c: Tangent(g1,g5) = 1.5708
    c: Perpendicular(g1,g2)
FEATURE [PartDesign::Revolution] Revolution
  Angle = 360
  Angle2 = 60
  Axis = (0,0,1)
  Base = (0,0,0)
  Placement = pos=(0,0,0) rot=(1,1,1;2.0944rad)
  Profile = -> Sketch018
  ReferenceAxis = -> Sketch018 [V_Axis]
  Refine = true
  Reversed = true
  Suppressed = false
  Type = 0
FEATURE [PartDesign::Body] Body004  label="bouton"
  AllowCompound = false
  Group = -> [Sketch018,Revolution]
  Origin = -> Origin054
  Placement = pos=(-9,-23,32) rot=(0,0,1;0rad)
  Tip = -> Revolution
FEATURE [App::Link] Bottom  label="Bottom001"
  LinkPlacement = pos=(25.5157,-54.2242,7.05046) rot=(0,0,1;3.14159rad)
  LinkedObject = -> Body
  Placement = pos=(25.5157,-54.2242,7.05046) rot=(0,0,1;3.14159rad)
FEATURE [App::FeaturePython] GroundedJoint  # Assembly grounded joint (typed FeaturePython)
  ObjectToGround = -> Bottom
  Placement = pos=(25.5157,-54.2242,7.05046) rot=(0,0,1;3.14159rad)
FEATURE [App::Link] Front  label="Front001"
  LinkPlacement = pos=(25.0157,38.2758,7.35379) rot=(0,0,1;0rad)
  LinkedObject = -> Body001
  Placement = pos=(25.0157,38.2758,7.35379) rot=(0,0,1;0rad)
FEATURE [App::Link] PCB001
  LinkPlacement = pos=(52.0157,-9.39019,17.54) rot=(0,0,1;3.14159rad)
  LinkedObject = -> PCB
  Placement = pos=(52.0157,-9.39019,17.54) rot=(0,0,1;3.14159rad)
FEATURE [App::Link] Back  label="Back001"
  LinkPlacement = pos=(26.0157,-54.7242,7.06063) rot=(0,0,1;0rad)
  LinkedObject = -> Body002
  Placement = pos=(26.0157,-54.7242,7.06063) rot=(0,0,1;0rad)
FEATURE [App::Link] Top  label="Top001"
  LinkPlacement = pos=(25.5157,-54.2242,47.0736) rot=(0,1,0;3.14159rad)
  LinkedObject = -> Body003
  Placement = pos=(25.5157,-54.2242,47.0736) rot=(0,1,0;3.14159rad)
FEATURE [App::Link] bouton  label="bouton001"
  LinkPlacement = pos=(19.1506,-28.5672,25.84) rot=(0,0,1;4.71239rad)
  LinkedObject = -> Body004
  Placement = pos=(19.1506,-28.5672,25.84) rot=(0,0,1;4.71239rad)
FEATURE [App::Link] bouton001  label="bouton002"
  LinkPlacement = pos=(36.0157,-28.5672,25.92) rot=(0,0,1;4.71239rad)
  LinkedObject = -> Body004
  Placement = pos=(36.0157,-28.5672,25.92) rot=(0,0,1;4.71239rad)
FEATURE [PartDesign::Chamfer] Chamfer004
  Angle = 45
  Base = -> Chamfer003 [Face72,Face102]
  BaseFeature = -> Chamfer003
  ChamferType = 0
  FlipDirection = false
  Refine = true
  Size = 0.49
  Size2 = 1
  SupportTransform = false
  Suppressed = false
  UseAllEdges = false
FEATURE [PartDesign::Body] Body003  label="Top"
  AllowCompound = false
  Group = -> [Sketch011,Pad004,Sketch012,Pocket006,Sketch013,Pocket007,Sketch014,Pocket008,Mirrored003,Sketch015,Pad005,Mirrored004,Sketch016,Pad006,MultiTransform,Mirrored005,Mirrored006,Sketch017,Pocket009,Chamfer002,Fillet004,Fillet005,Chamfer003,Chamfer004]
  Origin = -> Origin053
  Placement = pos=(0,0,40) rot=(0,1,0;3.14159rad)
  Tip = -> Chamfer004
FEATURE [Sketcher::SketchObject] Sketch019
  ArcFitTolerance = 1e-06
  AttachmentSupport = -> [Fillet003]
  FullyConstrained = true
  MakeInternals = false
  MapMode = 5
  Placement = pos=(0,-48.5,-3.94e-14) rot=(1,0,0;1.5708rad)
  sketch-geometry (6):
    g0: ArcOfCircle CenterX=23 CenterY=24 CenterZ=0 NormalX=0 NormalY=0 NormalZ=1 AngleXU=0 Radius=4.8 StartAngle=5.29807 EndAngle=10.4099
    g1: Circle [constr] CenterX=23 CenterY=24 CenterZ=0 NormalX=0 NormalY=0 NormalZ=1 AngleXU=0 Radius=6.325
    g2: LineSegment StartX=20.3467 StartY=20 StartZ=0 EndX=25.6533 EndY=20 EndZ=0
    g3: Circle [constr] CenterX=-23 CenterY=24 CenterZ=0 NormalX=0 NormalY=0 NormalZ=1 AngleXU=0 Radius=6.325
    g4: ArcOfCircle CenterX=-23 CenterY=24 CenterZ=0 NormalX=0 NormalY=0 NormalZ=1 AngleXU=0 Radius=4.8 StartAngle=5.29807 EndAngle=10.4099
    g5: LineSegment StartX=-25.6533 StartY=20 StartZ=0 EndX=-20.3467 EndY=20 EndZ=0
  constraints (18):
    c: Diameter(g0) = 9.6
    c: Diameter(g1) = 12.65
    c: Coincident(g1,g0)
    c: Distance(g0,g2) = 4
    c: DistanceY(g-1,g0) = 24
    c: DistanceX(g-1,g0) = 23
    c: Coincident(g0,g2)
    c: Coincident(g0,g2)
    c: Coincident(g4,g3)
    c: Equal(g4,g0)
    c: Equal(g3,g1)
    c: Horizontal(g3,g0)
    c: Horizontal(g5)
    c: Horizontal(g5,g0)
    c: Coincident(g4,g5)
    c: Coincident(g4,g5)
    c: DistanceX(g3,g-1) = 23
    c: Horizontal(g2)
FEATURE [PartDesign::Pocket] Pocket010
  BaseFeature = -> Fillet003
  Direction = (0,1,-2e-16)
  Length = 5
  Length2 = 5
  Placement = pos=(0,-47,-3.94e-14) rot=(1,0,0;1.5708rad)
  Profile = -> Sketch019
  ReferenceAxis = -> Sketch019 [N_Axis]
  Refine = true
  Suppressed = false
  Type = 1
FEATURE [PartDesign::Body] Body002  label="Back"
  AllowCompound = false
  Group = -> [DatumPlane001,Sketch010,Pad003,Fillet003,Sketch019,Pocket010]
  Origin = -> Origin052
  Tip = -> Pocket010
FEATURE [App::FeaturePython] Joint  label="Slider"  # Assembly joint (typed FeaturePython)
  Activated = true
  AngleMax = 0
  AngleMin = 0
  Detach1 = false
  Detach2 = false
  Distance = 0
  Distance2 = 0
  EnableAngleMax = false
  EnableAngleMin = false
  EnableLengthMax = true
  EnableLengthMin = true
  JointType = 3 (Slider)
  LengthMax = 0
  LengthMin = -20
  Placement1 = pos=(48,5.334,0) rot=(0,0,1;0rad)
  Placement2 = pos=(21.5,-39.5,10) rot=(0,0,1;0rad)
  Reference1 = -> Assembly [PCB001.Board.Part__Feature.Edge247,PCB001.Board.Part__Feature.Edge247]
  Reference2 = -> Assembly [Bottom.Edge165,Bottom.Edge165]
FEATURE [App::FeaturePython] Joint001  label="Slider001"  # Assembly joint (typed FeaturePython)
  Activated = true
  AngleMax = 0
  AngleMin = 0
  Detach1 = false
  Detach2 = false
  Distance = 0
  Distance2 = 0
  EnableAngleMax = false
  EnableAngleMin = false
  EnableLengthMax = true
  EnableLengthMin = false
  JointType = 3 (Slider)
  LengthMax = -8.72598
  LengthMin = -8.72598
  Placement1 = pos=(-32.5,-43.5,19.5) rot=(0,0,1;0rad)
  Placement2 = pos=(33,-49,11) rot=(0,1,0;3.14159rad)
  Reference1 = -> Assembly [Front.Edge36,Front.Edge36]
  Reference2 = -> Assembly [Bottom.Edge81,Bottom.Edge81]
FEATURE [App::FeaturePython] Joint002  label="Slider002"  # Assembly joint (typed FeaturePython)
  Activated = true
  AngleMax = 0
  AngleMin = 0
  Detach1 = false
  Detach2 = false
  Distance = 0
  Distance2 = 0
  EnableAngleMax = false
  EnableAngleMin = false
  EnableLengthMax = true
  EnableLengthMin = false
  JointType = 3 (Slider)
  LengthMax = -8.51017
  LengthMin = 0
  Offset2 = pos=(0,0,0) rot=(0,0,1;3.14159rad)
  Placement1 = pos=(32.5,-48.5,19.5) rot=(0,0,1;0rad)
  Placement2 = pos=(-33,49,11) rot=(0,0,1;3.14159rad)
  Reference1 = -> Assembly [Back.Edge32,Back.Edge32]
  Reference2 = -> Assembly [Bottom.Edge59,Bottom.Edge59]
FEATURE [App::FeaturePython] Joint003  label="Slider003"  # Assembly joint (typed FeaturePython)
  Activated = true
  AngleMax = 0
  AngleMin = 0
  Detach1 = false
  Detach2 = false
  Distance = 0
  Distance2 = 0
  EnableAngleMax = false
  EnableAngleMin = false
  EnableLengthMax = false
  EnableLengthMin = true
  JointType = 3 (Slider)
  LengthMax = 0
  LengthMin = 0
  Placement1 = pos=(0,0,5) rot=(-0.707107,-0.707107,0;3.14159rad)
  Placement2 = pos=(0,0,0.3) rot=(0,1,0;3.14159rad)
  Reference1 = -> Assembly [bouton001.Edge4,bouton001.Edge4]
  Reference2 = -> Assembly [PCB001.SW1.Switch_TE_Connectivity_2_1825910_7_eec001.Part__Feature068.Face4,PCB001.SW1.Switch_TE_Connectivity_2_1825910_7_eec001.Part__Feature068.Edge1]
FEATURE [App::FeaturePython] Joint004  label="Slider004"  # Assembly joint (typed FeaturePython)
  Activated = true
  AngleMax = 0
  AngleMin = 0
  Detach1 = false
  Detach2 = false
  Distance = 0
  Distance2 = 0
  EnableAngleMax = false
  EnableAngleMin = false
  EnableLengthMax = true
  EnableLengthMin = false
  JointType = 3 (Slider)
  LengthMax = 0
  LengthMin = 0
  Placement1 = pos=(-3.6e-15,0,5) rot=(0,0,-1;1.5708rad)
  Placement2 = pos=(-1.13483,0,0.3) rot=(0,0,1;0rad)
  Reference1 = -> Assembly [bouton.Face2,bouton.Face2]
  Reference2 = -> Assembly [PCB001.SW2.Switch_TE_Connectivity_2_1825910_7_eec.Part__Feature043.Vertex4,PCB001.SW2.Switch_TE_Connectivity_2_1825910_7_eec.Part__Feature043.Vertex4]
FEATURE [App::FeaturePython] Joint005  label="Slider005"  # Assembly joint (typed FeaturePython)
  Activated = true
  AngleMax = 0
  AngleMin = 0
  Detach1 = false
  Detach2 = false
  Distance = 0
  Distance2 = 0
  EnableAngleMax = false
  EnableAngleMin = false
  EnableLengthMax = false
  EnableLengthMin = true
  JointType = 3 (Slider)
  LengthMax = 0
  LengthMin = 0.21976
  Placement1 = pos=(-32.5,-43.5,19.5) rot=(0,0,1;0rad)
  Placement2 = pos=(33,49,20) rot=(0,1,0;3.14159rad)
  Reference1 = -> Assembly [Front.Edge36,Front.Edge36]
  Reference2 = -> Assembly [Top.Edge64,Top.Vertex48]
FEATURE [Assembly::JointGroup] Joints
  Group = -> [GroundedJoint,Joint,Joint001,Joint002,Joint003,Joint004,Joint005]
FEATURE [Assembly::AssemblyObject] Assembly
  Group = -> [Joints,Bottom,GroundedJoint,Front,PCB001,Back,Top,bouton,bouton001,Joint,Joint001,Joint002,Joint003,Joint004,Joint005]
  Origin = -> Origin055
  Type = Assembly
FEATURE [Sketcher::SketchObject] Sketch020
  ArcFitTolerance = 0
  AttachmentSupport = -> [YZ_Plane056]
  FullyConstrained = true
  MakeInternals = false
  MapMode = 5
  Placement = pos=(0,0,0) rot=(0.57735,0.57735,0.57735;2.0944rad)
  sketch-geometry (8):
    g0: LineSegment StartX=1.8 StartY=0 StartZ=0 EndX=6.5 EndY=0 EndZ=0
    g1: ArcOfCircle CenterX=0 CenterY=10.3346 CenterZ=0 NormalX=0 NormalY=0 NormalZ=1 AngleXU=0 Radius=12 StartAngle=1.09468 EndAngle=1.5708
    g2: LineSegment StartX=0 StartY=22.3346 StartZ=0 EndX=0 EndY=5 EndZ=0
    g3: LineSegment StartX=1.8 StartY=5 StartZ=0 EndX=1.8 EndY=0 EndZ=0
    g4: LineSegment StartX=0 StartY=5 StartZ=0 EndX=1.8 EndY=5 EndZ=0
    g5: LineSegment StartX=6.5 StartY=17 StartZ=0 EndX=6.5 EndY=0 EndZ=0
    g6: LineSegment StartX=6.5 StartY=17 StartZ=0 EndX=5.5 EndY=17 EndZ=0
    g7: LineSegment StartX=5.5 StartY=17 StartZ=0 EndX=5.5 EndY=21 EndZ=0
  constraints (25):
    c: PointOnObject(g0,g-1)
    c: Horizontal(g0)
    c: PointOnObject(g1,g-2)
    c: Coincident(g1,g2)
    c: PointOnObject(g2,g-2)
    c: Coincident(g3,g0)
    c: Coincident(g2,g4)
    c: Horizontal(g4)
    c: Vertical(g3)
    c: Distance(g0,g-2) = 1.8
    c: DistanceX(g-1,g1) = 5.5
    c: DistanceY(g-1,g2) = 5
    c: Coincident(g3,g4)
    c: Coincident(g5,g0)
    c: Perpendicular(g1,g2)
    c: Distance(g0,g-1) = 6.5
    c: Vertical(g5)
    c: DistanceY(g3,g5) = 12
    c: Coincident(g5,g6)
    c: Horizontal(g6)
    c: Coincident(g6,g7)
    c: Coincident(g7,g1)
    c: Vertical(g7)
    c: Distance(g1,g4) = 16
    c: Radius(g1) = 12
FEATURE [PartDesign::Revolution] Revolution001
  Angle = 360
  Angle2 = 60
  Axis = (0,0,1)
  Base = (0,0,0)
  Placement = pos=(0,0,0) rot=(1,1,1;2.0944rad)
  Profile = -> Sketch020
  ReferenceAxis = -> Sketch020 [V_Axis]
  Refine = true
  Reversed = true
  Suppressed = false
  Type = 0
FEATURE [PartDesign::Body] Body005  label="bouton003"
  AllowCompound = false
  Group = -> [Sketch020,Revolution001]
  Origin = -> Origin056
  Placement = pos=(-9,-23,32) rot=(0,0,1;0rad)
  Tip = -> Revolution001
